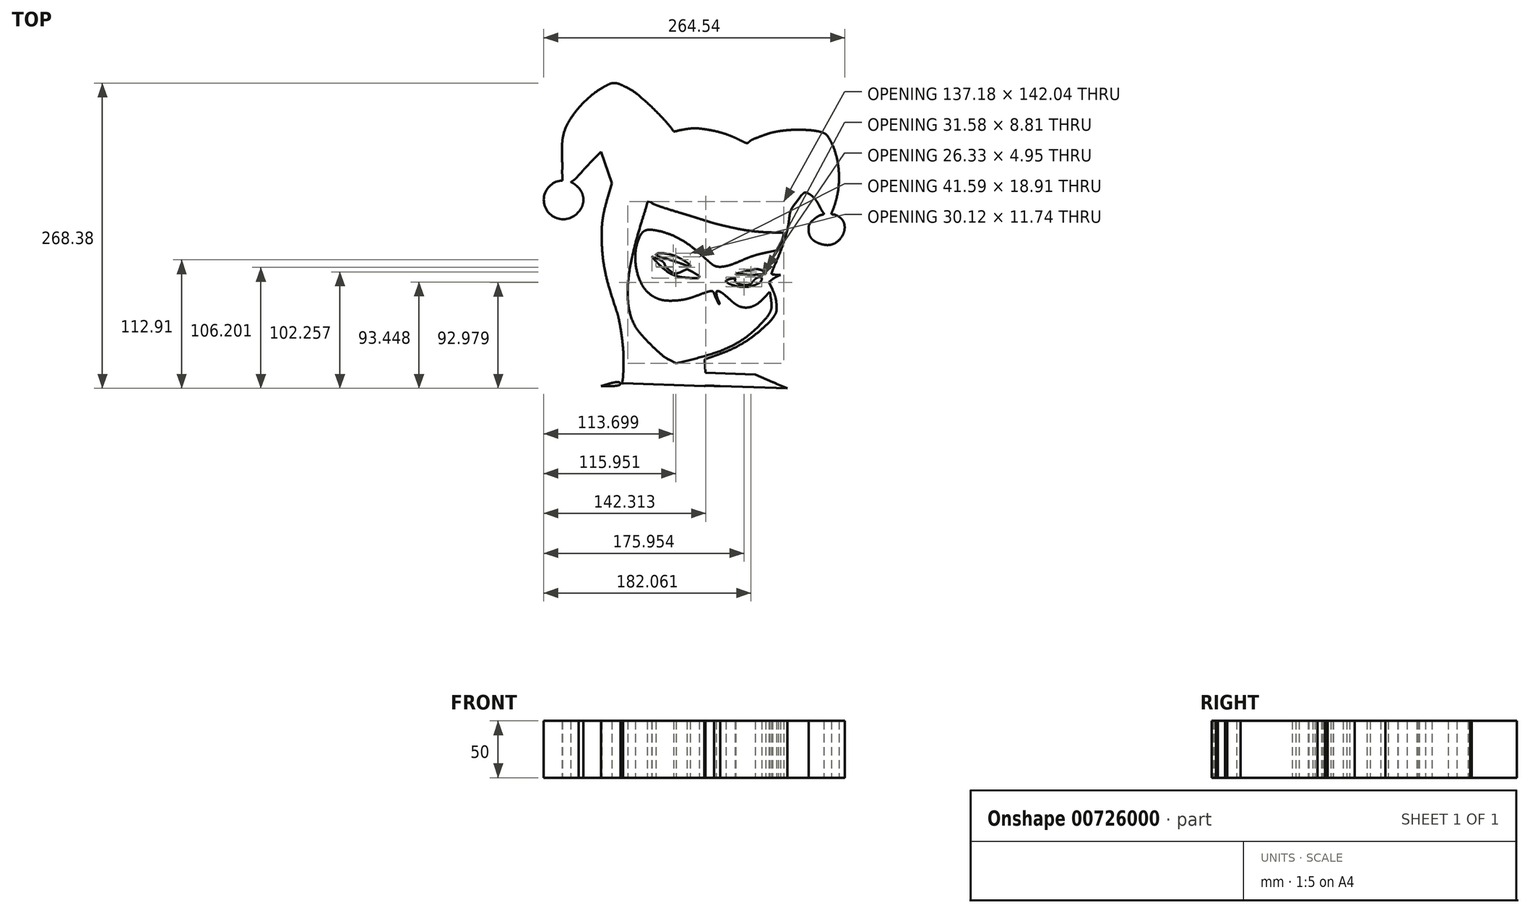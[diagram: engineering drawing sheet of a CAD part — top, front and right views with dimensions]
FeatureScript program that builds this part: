
annotation { "Feature Type Name" : "Feature", "Feature Type Description" : "" }
export const myFeature = defineFeature(function(context is Context, id is Id, definition is map)
    precondition{}
    {
        {
            var Q0;
            Q0=qCreatedBy(makeId("Top.planeOp"),FACE);
            var sketch = newSketch(context, id + "F0", { "sketchPlane" : qUnion([Q0])});
            skArc(sketch, "E0", {"start": v(-81.32, 129.17) * mm, "mid": v(-87.44, 125.11) * mm, "end": v(-93.17, 120.52) * mm});
            skArc(sketch, "E1", {"start": v(-93.17, 120.52) * mm, "mid": v(-98.64, 115.3) * mm, "end": v(-103.66, 109.63) * mm});
            skArc(sketch, "E2", {"start": v(-103.66, 109.63) * mm, "mid": v(-107.89, 103.97) * mm, "end": v(-111.61, 97.95) * mm});
            skArc(sketch, "E3", {"start": v(-111.61, 97.95) * mm, "mid": v(-114.1, 92.6) * mm, "end": v(-115.78, 86.95) * mm});
            skArc(sketch, "E4", {"start": v(-115.78, 86.95) * mm, "mid": v(-116.39, 83.45) * mm, "end": v(-116.67, 79.91) * mm});
            skArc(sketch, "E5", {"start": v(-116.67, 79.91) * mm, "mid": v(-116.8, 74.58) * mm, "end": v(-116.78, 69.25) * mm});
            skArc(sketch, "E6", {"start": v(-116.78, 69.25) * mm, "mid": v(-116.63, 64) * mm, "end": v(-116.35, 58.76) * mm});
            skArc(sketch, "E7", {"start": v(-116.35, 58.76) * mm, "mid": v(-116.71, 55.94) * mm, "end": v(-116.58, 53.1) * mm});
            skArc(sketch, "E8", {"start": v(-113.81, 56.72) * mm, "mid": v(-113.72, 62.46) * mm, "end": v(-113.64, 68.2) * mm});
            skArc(sketch, "E9", {"start": v(-113.64, 68.2) * mm, "mid": v(-113.48, 73.22) * mm, "end": v(-113.14, 78.23) * mm});
            skArc(sketch, "E10", {"start": v(-113.14, 78.23) * mm, "mid": v(-112.64, 82.07) * mm, "end": v(-111.84, 85.86) * mm});
            skArc(sketch, "E11", {"start": v(-111.84, 85.86) * mm, "mid": v(-110.77, 89.4) * mm, "end": v(-109.4, 92.83) * mm});
            skArc(sketch, "E12", {"start": v(-109.4, 92.83) * mm, "mid": v(-107.48, 96.82) * mm, "end": v(-105.36, 100.7) * mm});
            skArc(sketch, "E13", {"start": v(-105.36, 100.7) * mm, "mid": v(-102.38, 105.27) * mm, "end": v(-98.93, 109.5) * mm});
            skArc(sketch, "E14", {"start": v(-98.93, 109.5) * mm, "mid": v(-93.73, 114.95) * mm, "end": v(-88.31, 120.18) * mm});
            skArc(sketch, "E15", {"start": v(-88.31, 120.18) * mm, "mid": v(-82.87, 125.07) * mm, "end": v(-77.28, 129.78) * mm});
            skArc(sketch, "E16", {"start": v(-77.28, 129.78) * mm, "mid": v(-74.74, 131.2) * mm, "end": v(-71.87, 131.7) * mm});
            skArc(sketch, "E17", {"start": v(-71.87, 131.7) * mm, "mid": v(-70.1, 131.5) * mm, "end": v(-68.4, 130.9) * mm});
            skArc(sketch, "E18", {"start": v(-68.4, 130.9) * mm, "mid": v(-64.88, 129.08) * mm, "end": v(-61.4, 127.18) * mm});
            skArc(sketch, "E19", {"start": v(-61.4, 127.18) * mm, "mid": v(-57.7, 125) * mm, "end": v(-54.1, 122.7) * mm});
            skArc(sketch, "E20", {"start": v(-54.1, 122.7) * mm, "mid": v(-51.08, 120.58) * mm, "end": v(-48.19, 118.3) * mm});
            skArc(sketch, "E21", {"start": v(-48.19, 118.3) * mm, "mid": v(-43.26, 113.98) * mm, "end": v(-38.55, 109.45) * mm});
            skArc(sketch, "E22", {"start": v(-38.55, 109.45) * mm, "mid": v(-33.2, 103.92) * mm, "end": v(-28.02, 98.23) * mm});
            skArc(sketch, "E23", {"start": v(-28.02, 98.23) * mm, "mid": v(-23.22, 92.72) * mm, "end": v(-18.5, 87.13) * mm});
            skArc(sketch, "E24", {"start": v(-18.5, 87.13) * mm, "mid": v(-17.44, 85.27) * mm, "end": v(-17.07, 83.16) * mm});
            skArc(sketch, "E25", {"start": v(-17.07, 83.16) * mm, "mid": v(-17.14, 82.51) * mm, "end": v(-17.33, 81.9) * mm});
            skArc(sketch, "E26", {"start": v(-17.33, 81.9) * mm, "mid": v(-17.96, 80.48) * mm, "end": v(-18.61, 79.08) * mm});
            skArc(sketch, "E27", {"start": v(-18.61, 79.08) * mm, "mid": v(-19.44, 77.4) * mm, "end": v(-20.31, 75.75) * mm});
            skArc(sketch, "E28", {"start": v(-20.31, 75.75) * mm, "mid": v(-21.3, 73.96) * mm, "end": v(-22.32, 72.2) * mm});
            skArc(sketch, "E29", {"start": v(-22.32, 72.2) * mm, "mid": v(-25.2, 67.7) * mm, "end": v(-28.37, 63.39) * mm});
            skArc(sketch, "E30", {"start": v(-28.37, 63.39) * mm, "mid": v(-32.27, 58.69) * mm, "end": v(-36.38, 54.17) * mm});
            skArc(sketch, "E31", {"start": v(-36.38, 54.17) * mm, "mid": v(-40.75, 49.77) * mm, "end": v(-45.31, 45.58) * mm});
            skArc(sketch, "E32", {"start": v(-45.31, 45.58) * mm, "mid": v(-49.65, 42) * mm, "end": v(-54.2, 38.67) * mm});
            skArc(sketch, "E33", {"start": v(-54.2, 38.67) * mm, "mid": v(-56.08, 37.36) * mm, "end": v(-57.94, 36) * mm});
            skArc(sketch, "E34", {"start": v(-57.94, 36) * mm, "mid": v(-59.29, 34.97) * mm, "end": v(-60.59, 33.88) * mm});
            skArc(sketch, "E35", {"start": v(-60.59, 33.88) * mm, "mid": v(-61.47, 33.07) * mm, "end": v(-62.31, 32.22) * mm});
            skArc(sketch, "E36", {"start": v(-62.31, 32.22) * mm, "mid": v(-62.44, 31.96) * mm, "end": v(-62.4, 31.67) * mm});
            skArc(sketch, "E37", {"start": v(-60.44, 31.27) * mm, "mid": v(-57.35, 33) * mm, "end": v(-54.3, 34.83) * mm});
            skArc(sketch, "E38", {"start": v(-54.3, 34.83) * mm, "mid": v(-50.86, 37.06) * mm, "end": v(-47.5, 39.45) * mm});
            skArc(sketch, "E39", {"start": v(-47.5, 39.45) * mm, "mid": v(-44.24, 42) * mm, "end": v(-41.07, 44.67) * mm});
            skArc(sketch, "E40", {"start": v(-41.07, 44.67) * mm, "mid": v(-40.56, 45.12) * mm, "end": v(-40.04, 45.57) * mm});
            skArc(sketch, "E41", {"start": v(-40.04, 45.57) * mm, "mid": v(-39.53, 46) * mm, "end": v(-39, 46.43) * mm});
            skArc(sketch, "E42", {"start": v(-39, 46.43) * mm, "mid": v(-38.56, 46.79) * mm, "end": v(-38.1, 47.15) * mm});
            skArc(sketch, "E43", {"start": v(-38.1, 47.15) * mm, "mid": v(-37.83, 47.35) * mm, "end": v(-37.56, 47.54) * mm});
            skArc(sketch, "E44", {"start": v(-37.56, 47.54) * mm, "mid": v(-37.22, 47.8) * mm, "end": v(-36.9, 48.08) * mm});
            skArc(sketch, "E45", {"start": v(-36.9, 48.08) * mm, "mid": v(-35.83, 49.22) * mm, "end": v(-34.75, 50.36) * mm});
            skArc(sketch, "E46", {"start": v(-34.75, 50.36) * mm, "mid": v(-33.48, 51.72) * mm, "end": v(-32.23, 53.1) * mm});
            skArc(sketch, "E47", {"start": v(-32.23, 53.1) * mm, "mid": v(-30.82, 54.64) * mm, "end": v(-29.43, 56.2) * mm});
            skArc(sketch, "E48", {"start": v(-29.43, 56.2) * mm, "mid": v(-25.77, 60.56) * mm, "end": v(-22.36, 65.1) * mm});
            skArc(sketch, "E49", {"start": v(-22.36, 65.1) * mm, "mid": v(-19.43, 69.57) * mm, "end": v(-16.8, 74.22) * mm});
            skArc(sketch, "E50", {"start": v(-16.8, 74.22) * mm, "mid": v(-14.97, 78.05) * mm, "end": v(-13.4, 81.99) * mm});
            skArc(sketch, "E51", {"start": v(-13.4, 81.99) * mm, "mid": v(-13.34, 83.75) * mm, "end": v(-14.35, 85.19) * mm});
            skArc(sketch, "E52", {"start": v(-14.35, 85.19) * mm, "mid": v(-14.7, 85.49) * mm, "end": v(-15.03, 85.82) * mm});
            skArc(sketch, "E53", {"start": v(-15.03, 85.82) * mm, "mid": v(-15.55, 86.42) * mm, "end": v(-16.06, 87.04) * mm});
            skArc(sketch, "E54", {"start": v(-16.06, 87.04) * mm, "mid": v(-16.64, 87.77) * mm, "end": v(-17.2, 88.51) * mm});
            skArc(sketch, "E55", {"start": v(-17.2, 88.51) * mm, "mid": v(-17.76, 89.28) * mm, "end": v(-18.3, 90.07) * mm});
            skArc(sketch, "E56", {"start": v(-18.3, 90.07) * mm, "mid": v(-22.18, 95.38) * mm, "end": v(-26.43, 100.4) * mm});
            skArc(sketch, "E57", {"start": v(-26.43, 100.4) * mm, "mid": v(-32.2, 106.5) * mm, "end": v(-38.19, 112.41) * mm});
            skArc(sketch, "E58", {"start": v(-38.19, 112.41) * mm, "mid": v(-44.17, 117.91) * mm, "end": v(-50.34, 123.21) * mm});
            skArc(sketch, "E59", {"start": v(-50.34, 123.21) * mm, "mid": v(-54.65, 126.4) * mm, "end": v(-59.3, 129.09) * mm});
            skArc(sketch, "E60", {"start": v(-59.3, 129.09) * mm, "mid": v(-62.9, 130.82) * mm, "end": v(-66.58, 132.41) * mm});
            skArc(sketch, "E61", {"start": v(-66.58, 132.41) * mm, "mid": v(-68.75, 133.07) * mm, "end": v(-71, 133.3) * mm});
            skArc(sketch, "E62", {"start": v(-71, 133.3) * mm, "mid": v(-73.15, 133.07) * mm, "end": v(-75.2, 132.4) * mm});
            skArc(sketch, "E63", {"start": v(-75.2, 132.4) * mm, "mid": v(-78.3, 130.87) * mm, "end": v(-81.32, 129.17) * mm});
            skArc(sketch, "E64", {"start": v(-9.05, 92.56) * mm, "mid": v(-13.84, 91.64) * mm, "end": v(-18.58, 90.47) * mm});
            skLineSegment(sketch, "E65", {"start": v(11.05, 89.96) * mm, "end": v(14.74, 87) * mm});
            skArc(sketch, "E66", {"start": v(14.74, 87) * mm, "mid": v(15.68, 86.18) * mm, "end": v(16.55, 85.29) * mm});
            skArc(sketch, "E67", {"start": v(16.55, 85.29) * mm, "mid": v(17.85, 83.8) * mm, "end": v(19.1, 82.3) * mm});
            skArc(sketch, "E68", {"start": v(19.1, 82.3) * mm, "mid": v(20.5, 80.55) * mm, "end": v(21.86, 78.77) * mm});
            skArc(sketch, "E69", {"start": v(21.86, 78.77) * mm, "mid": v(23.17, 76.97) * mm, "end": v(24.43, 75.14) * mm});
            skLineSegment(sketch, "E70", {"start": v(30.43, 66.23) * mm, "end": v(30.26, 48.22) * mm});
            skArc(sketch, "E71", {"start": v(30.26, 48.22) * mm, "mid": v(30.19, 43.8) * mm, "end": v(30.07, 39.4) * mm});
            skArc(sketch, "E72", {"start": v(30.07, 39.4) * mm, "mid": v(29.91, 35.74) * mm, "end": v(29.68, 32.09) * mm});
            skArc(sketch, "E73", {"start": v(29.68, 32.09) * mm, "mid": v(29.42, 28.95) * mm, "end": v(29.08, 25.82) * mm});
            skArc(sketch, "E74", {"start": v(29.08, 25.82) * mm, "mid": v(28.69, 23) * mm, "end": v(28.21, 20.2) * mm});
            skArc(sketch, "E75", {"start": v(28.21, 20.2) * mm, "mid": v(27.6, 17.05) * mm, "end": v(26.98, 13.9) * mm});
            skArc(sketch, "E76", {"start": v(26.98, 13.9) * mm, "mid": v(26.68, 12.75) * mm, "end": v(26.26, 11.64) * mm});
            skArc(sketch, "E77", {"start": v(26.26, 11.64) * mm, "mid": v(25.88, 11.1) * mm, "end": v(25.33, 10.7) * mm});
            skArc(sketch, "E78", {"start": v(25.33, 10.7) * mm, "mid": v(24.63, 10.49) * mm, "end": v(23.88, 10.46) * mm});
            skArc(sketch, "E79", {"start": v(23.88, 10.46) * mm, "mid": v(22.5, 10.67) * mm, "end": v(21.13, 11) * mm});
            skArc(sketch, "E80", {"start": v(21.13, 11) * mm, "mid": v(16.22, 12.45) * mm, "end": v(11.31, 13.91) * mm});
            skArc(sketch, "E81", {"start": v(11.31, 13.91) * mm, "mid": v(4.2, 16.06) * mm, "end": v(-2.9, 18.24) * mm});
            skArc(sketch, "E82", {"start": v(-25.89, 25.38) * mm, "mid": v(-28.07, 26.05) * mm, "end": v(-30.26, 26.7) * mm});
            skArc(sketch, "E83", {"start": v(-30.26, 26.7) * mm, "mid": v(-32.14, 27.22) * mm, "end": v(-34.03, 27.72) * mm});
            skArc(sketch, "E84", {"start": v(-37.72, 28.39) * mm, "mid": v(-37.88, 27.88) * mm, "end": v(-37.55, 27.45) * mm});
            skArc(sketch, "E85", {"start": v(-37.55, 27.45) * mm, "mid": v(-35.57, 26.58) * mm, "end": v(-33.56, 25.79) * mm});
            skArc(sketch, "E86", {"start": v(-33.56, 25.79) * mm, "mid": v(-30.1, 24.54) * mm, "end": v(-26.6, 23.38) * mm});
            skArc(sketch, "E87", {"start": v(-26.6, 23.38) * mm, "mid": v(-19.94, 21.3) * mm, "end": v(-13.27, 19.23) * mm});
            skArc(sketch, "E88", {"start": v(-13.27, 19.23) * mm, "mid": v(-9.06, 17.93) * mm, "end": v(-4.85, 16.64) * mm});
            skArc(sketch, "E89", {"start": v(-4.85, 16.64) * mm, "mid": v(-0.76, 15.38) * mm, "end": v(3.34, 14.11) * mm});
            skArc(sketch, "E90", {"start": v(3.34, 14.11) * mm, "mid": v(6.84, 13.03) * mm, "end": v(10.35, 11.94) * mm});
            skArc(sketch, "E91", {"start": v(10.35, 11.94) * mm, "mid": v(12.27, 11.35) * mm, "end": v(14.2, 10.74) * mm});
            skArc(sketch, "E92", {"start": v(14.2, 10.74) * mm, "mid": v(15.97, 10.2) * mm, "end": v(17.77, 9.72) * mm});
            skArc(sketch, "E93", {"start": v(17.77, 9.72) * mm, "mid": v(20.53, 9.01) * mm, "end": v(23.3, 8.33) * mm});
            skArc(sketch, "E94", {"start": v(23.3, 8.33) * mm, "mid": v(26.43, 7.58) * mm, "end": v(29.56, 6.86) * mm});
            skArc(sketch, "E95", {"start": v(29.56, 6.86) * mm, "mid": v(32.62, 6.18) * mm, "end": v(35.7, 5.52) * mm});
            skArc(sketch, "E96", {"start": v(35.7, 5.52) * mm, "mid": v(40.58, 4.57) * mm, "end": v(45.48, 3.75) * mm});
            skArc(sketch, "E97", {"start": v(45.48, 3.75) * mm, "mid": v(50.3, 3.1) * mm, "end": v(55.12, 2.58) * mm});
            skArc(sketch, "E98", {"start": v(55.12, 2.58) * mm, "mid": v(60.3, 2.18) * mm, "end": v(65.47, 1.92) * mm});
            skArc(sketch, "E99", {"start": v(65.47, 1.92) * mm, "mid": v(71.47, 1.76) * mm, "end": v(77.47, 1.7) * mm});
            skArc(sketch, "E100", {"start": v(77.47, 1.7) * mm, "mid": v(77.8, 1.58) * mm, "end": v(78, 1.28) * mm});
            skArc(sketch, "E101", {"start": v(78, 1.28) * mm, "mid": v(78.07, 0.7) * mm, "end": v(78.03, 0.13) * mm});
            skArc(sketch, "E102", {"start": v(78.03, 0.13) * mm, "mid": v(77.8, -0.96) * mm, "end": v(77.48, -2.03) * mm});
            skArc(sketch, "E103", {"start": v(77.48, -2.03) * mm, "mid": v(76.81, -4) * mm, "end": v(76.12, -5.96) * mm});
            skLineSegment(sketch, "E104", {"start": v(76.12, -5.96) * mm, "end": v(73.34, -13.62) * mm});
            skLineSegment(sketch, "E105", {"start": v(73.34, -13.62) * mm, "end": v(64.38, -15.47) * mm});
            skArc(sketch, "E106", {"start": v(64.38, -15.47) * mm, "mid": v(60.62, -16.27) * mm, "end": v(56.88, -17.13) * mm});
            skArc(sketch, "E107", {"start": v(56.88, -17.13) * mm, "mid": v(54.29, -17.8) * mm, "end": v(51.73, -18.56) * mm});
            skArc(sketch, "E108", {"start": v(51.73, -18.56) * mm, "mid": v(49.08, -19.48) * mm, "end": v(46.46, -20.49) * mm});
            skArc(sketch, "E109", {"start": v(46.46, -20.49) * mm, "mid": v(42.37, -22.18) * mm, "end": v(38.29, -23.92) * mm});
            skArc(sketch, "E110", {"start": v(38.29, -23.92) * mm, "mid": v(34.67, -25.4) * mm, "end": v(31, -26.71) * mm});
            skArc(sketch, "E111", {"start": v(31, -26.71) * mm, "mid": v(28.1, -27.55) * mm, "end": v(25.14, -28.12) * mm});
            skArc(sketch, "E112", {"start": v(25.14, -28.12) * mm, "mid": v(22.78, -28.33) * mm, "end": v(20.4, -28.26) * mm});
            skArc(sketch, "E113", {"start": v(20.4, -28.26) * mm, "mid": v(18.45, -27.9) * mm, "end": v(16.61, -27.14) * mm});
            skArc(sketch, "E114", {"start": v(16.61, -27.14) * mm, "mid": v(15.96, -26.76) * mm, "end": v(15.35, -26.3) * mm});
            skArc(sketch, "E115", {"start": v(15.35, -26.3) * mm, "mid": v(14.04, -25.24) * mm, "end": v(12.75, -24.15) * mm});
            skArc(sketch, "E116", {"start": v(12.75, -24.15) * mm, "mid": v(11.22, -22.83) * mm, "end": v(9.7, -21.5) * mm});
            skArc(sketch, "E117", {"start": v(9.7, -21.5) * mm, "mid": v(8.1, -20.04) * mm, "end": v(6.52, -18.57) * mm});
            skArc(sketch, "E118", {"start": v(6.52, -18.57) * mm, "mid": v(1.86, -14.42) * mm, "end": v(-3.01, -10.51) * mm});
            skArc(sketch, "E119", {"start": v(-3.01, -10.51) * mm, "mid": v(-7.68, -7.2) * mm, "end": v(-12.56, -4.22) * mm});
            skArc(sketch, "E120", {"start": v(-12.56, -4.22) * mm, "mid": v(-17.29, -1.76) * mm, "end": v(-22.18, 0.35) * mm});
            skArc(sketch, "E121", {"start": v(-22.18, 0.35) * mm, "mid": v(-27.02, 2) * mm, "end": v(-31.97, 3.25) * mm});
            skArc(sketch, "E122", {"start": v(-31.97, 3.25) * mm, "mid": v(-35.4, 3.86) * mm, "end": v(-38.87, 4.28) * mm});
            skArc(sketch, "E123", {"start": v(-38.87, 4.28) * mm, "mid": v(-41.08, 4.25) * mm, "end": v(-43.25, 3.77) * mm});
            skArc(sketch, "E124", {"start": v(-43.25, 3.77) * mm, "mid": v(-44.94, 2.93) * mm, "end": v(-46.33, 1.66) * mm});
            skArc(sketch, "E125", {"start": v(-46.33, 1.66) * mm, "mid": v(-47.73, -0.28) * mm, "end": v(-48.84, -2.4) * mm});
            skArc(sketch, "E126", {"start": v(-48.84, -2.4) * mm, "mid": v(-51.16, -9.17) * mm, "end": v(-52.28, -16.24) * mm});
            skArc(sketch, "E127", {"start": v(-52.28, -16.24) * mm, "mid": v(-52.28, -23.84) * mm, "end": v(-51.2, -31.36) * mm});
            skArc(sketch, "E128", {"start": v(-51.2, -31.36) * mm, "mid": v(-49.11, -38.28) * mm, "end": v(-46.02, -44.8) * mm});
            skArc(sketch, "E129", {"start": v(-46.02, -44.8) * mm, "mid": v(-42.34, -49.78) * mm, "end": v(-37.58, -53.75) * mm});
            skArc(sketch, "E130", {"start": v(-37.58, -53.75) * mm, "mid": v(-35.43, -55.03) * mm, "end": v(-33.19, -56.11) * mm});
            skArc(sketch, "E131", {"start": v(-33.19, -56.11) * mm, "mid": v(-31, -56.93) * mm, "end": v(-28.75, -57.52) * mm});
            skArc(sketch, "E132", {"start": v(-28.75, -57.52) * mm, "mid": v(-26.2, -57.93) * mm, "end": v(-23.62, -58.12) * mm});
            skArc(sketch, "E133", {"start": v(-23.62, -58.12) * mm, "mid": v(-20.34, -58.14) * mm, "end": v(-17.07, -58.01) * mm});
            skArc(sketch, "E134", {"start": v(-17.07, -58.01) * mm, "mid": v(-14.77, -57.83) * mm, "end": v(-12.47, -57.57) * mm});
            skArc(sketch, "E135", {"start": v(-12.47, -57.57) * mm, "mid": v(-10.35, -57.23) * mm, "end": v(-8.24, -56.8) * mm});
            skArc(sketch, "E136", {"start": v(-8.24, -56.8) * mm, "mid": v(-6.02, -56.26) * mm, "end": v(-3.82, -55.62) * mm});
            skArc(sketch, "E137", {"start": v(-3.82, -55.62) * mm, "mid": v(-1.18, -54.75) * mm, "end": v(1.43, -53.83) * mm});
            skArc(sketch, "E138", {"start": v(1.43, -53.83) * mm, "mid": v(5.95, -52.2) * mm, "end": v(10.48, -50.57) * mm});
            skArc(sketch, "E139", {"start": v(10.48, -50.57) * mm, "mid": v(12.13, -50.06) * mm, "end": v(13.83, -49.67) * mm});
            skArc(sketch, "E140", {"start": v(13.83, -49.67) * mm, "mid": v(14.7, -49.63) * mm, "end": v(15.53, -49.84) * mm});
            skArc(sketch, "E141", {"start": v(15.53, -49.84) * mm, "mid": v(16.16, -50.28) * mm, "end": v(16.55, -50.93) * mm});
            skArc(sketch, "E142", {"start": v(16.55, -50.93) * mm, "mid": v(17.23, -52.8) * mm, "end": v(17.97, -54.66) * mm});
            skArc(sketch, "E143", {"start": v(17.97, -54.66) * mm, "mid": v(18.71, -56.4) * mm, "end": v(19.52, -58.11) * mm});
            skArc(sketch, "E144", {"start": v(19.52, -58.11) * mm, "mid": v(20.24, -59.55) * mm, "end": v(20.99, -60.97) * mm});
            skArc(sketch, "E145", {"start": v(20.99, -60.97) * mm, "mid": v(21.23, -61.14) * mm, "end": v(21.51, -61.04) * mm});
            skArc(sketch, "E146", {"start": v(21.51, -61.04) * mm, "mid": v(21.63, -60.86) * mm, "end": v(21.64, -60.65) * mm});
            skArc(sketch, "E147", {"start": v(21.64, -60.65) * mm, "mid": v(21.56, -60.2) * mm, "end": v(21.45, -59.75) * mm});
            skArc(sketch, "E148", {"start": v(21.45, -59.75) * mm, "mid": v(21.27, -59.2) * mm, "end": v(21.06, -58.65) * mm});
            skArc(sketch, "E149", {"start": v(21.06, -58.65) * mm, "mid": v(20.8, -58.04) * mm, "end": v(20.5, -57.44) * mm});
            skArc(sketch, "E150", {"start": v(20.5, -57.44) * mm, "mid": v(20.18, -56.77) * mm, "end": v(19.9, -56.08) * mm});
            skArc(sketch, "E151", {"start": v(19.9, -56.08) * mm, "mid": v(19.63, -55.3) * mm, "end": v(19.4, -54.52) * mm});
            skArc(sketch, "E152", {"start": v(19.4, -54.52) * mm, "mid": v(19.2, -53.76) * mm, "end": v(19.04, -53) * mm});
            skArc(sketch, "E153", {"start": v(19.04, -53) * mm, "mid": v(18.96, -52.4) * mm, "end": v(18.93, -51.78) * mm});
            skArc(sketch, "E154", {"start": v(18.93, -51.78) * mm, "mid": v(18.95, -51.07) * mm, "end": v(19, -50.36) * mm});
            skArc(sketch, "E155", {"start": v(19, -50.36) * mm, "mid": v(19.11, -50.02) * mm, "end": v(19.33, -49.75) * mm});
            skArc(sketch, "E156", {"start": v(19.33, -49.75) * mm, "mid": v(19.62, -49.59) * mm, "end": v(19.95, -49.57) * mm});
            skArc(sketch, "E157", {"start": v(19.95, -49.57) * mm, "mid": v(20.57, -49.68) * mm, "end": v(21.18, -49.84) * mm});
            skArc(sketch, "E158", {"start": v(21.18, -49.84) * mm, "mid": v(21.73, -50.03) * mm, "end": v(22.25, -50.29) * mm});
            skArc(sketch, "E159", {"start": v(22.25, -50.29) * mm, "mid": v(22.96, -50.69) * mm, "end": v(23.65, -51.12) * mm});
            skArc(sketch, "E160", {"start": v(23.65, -51.12) * mm, "mid": v(24.4, -51.62) * mm, "end": v(25.12, -52.15) * mm});
            skArc(sketch, "E161", {"start": v(25.12, -52.15) * mm, "mid": v(25.78, -52.68) * mm, "end": v(26.43, -53.24) * mm});
            skArc(sketch, "E162", {"start": v(26.43, -53.24) * mm, "mid": v(28.9, -55.47) * mm, "end": v(31.37, -57.68) * mm});
            skArc(sketch, "E163", {"start": v(31.37, -57.68) * mm, "mid": v(32.77, -58.9) * mm, "end": v(34.22, -60.06) * mm});
            skArc(sketch, "E164", {"start": v(34.22, -60.06) * mm, "mid": v(35.27, -60.85) * mm, "end": v(36.37, -61.59) * mm});
            skArc(sketch, "E165", {"start": v(36.37, -61.59) * mm, "mid": v(37.45, -62.22) * mm, "end": v(38.57, -62.8) * mm});
            skArc(sketch, "E166", {"start": v(38.57, -62.8) * mm, "mid": v(41.25, -63.76) * mm, "end": v(44.06, -64.18) * mm});
            skArc(sketch, "E167", {"start": v(44.06, -64.18) * mm, "mid": v(46.96, -64.07) * mm, "end": v(49.8, -63.43) * mm});
            skArc(sketch, "E168", {"start": v(49.8, -63.43) * mm, "mid": v(52.79, -62.18) * mm, "end": v(55.55, -60.47) * mm});
            skArc(sketch, "E169", {"start": v(55.55, -60.47) * mm, "mid": v(58.46, -58.1) * mm, "end": v(61.12, -55.43) * mm});
            skLineSegment(sketch, "E170", {"start": v(61.12, -55.43) * mm, "end": v(65.76, -50.26) * mm});
            skLineSegment(sketch, "E171", {"start": v(65.76, -50.26) * mm, "end": v(66.3, -53.03) * mm});
            skArc(sketch, "E172", {"start": v(66.3, -53.03) * mm, "mid": v(66.97, -57.23) * mm, "end": v(67.4, -61.47) * mm});
            skArc(sketch, "E173", {"start": v(67.4, -61.47) * mm, "mid": v(67.33, -64.2) * mm, "end": v(66.7, -66.85) * mm});
            skArc(sketch, "E174", {"start": v(66.7, -66.85) * mm, "mid": v(65.49, -69.51) * mm, "end": v(63.83, -71.92) * mm});
            skArc(sketch, "E175", {"start": v(63.83, -71.92) * mm, "mid": v(60.46, -75.86) * mm, "end": v(56.95, -79.67) * mm});
            skArc(sketch, "E176", {"start": v(56.95, -79.67) * mm, "mid": v(51.35, -85.06) * mm, "end": v(45.32, -89.96) * mm});
            skArc(sketch, "E177", {"start": v(45.32, -89.96) * mm, "mid": v(39, -94.24) * mm, "end": v(32.33, -97.94) * mm});
            skArc(sketch, "E178", {"start": v(32.33, -97.94) * mm, "mid": v(24.46, -101.5) * mm, "end": v(16.35, -104.44) * mm});
            skArc(sketch, "E179", {"start": v(16.35, -104.44) * mm, "mid": v(5.97, -107.56) * mm, "end": v(-4.52, -110.27) * mm});
            skLineSegment(sketch, "E180", {"start": v(-4.52, -110.27) * mm, "end": v(-16.48, -113.12) * mm});
            skLineSegment(sketch, "E181", {"start": v(-16.48, -113.12) * mm, "end": v(-22.52, -110.1) * mm});
            skArc(sketch, "E182", {"start": v(-22.52, -110.1) * mm, "mid": v(-26.18, -107.99) * mm, "end": v(-29.53, -105.41) * mm});
            skArc(sketch, "E183", {"start": v(-29.53, -105.41) * mm, "mid": v(-34.53, -100.88) * mm, "end": v(-39.37, -96.19) * mm});
            skArc(sketch, "E184", {"start": v(-39.37, -96.19) * mm, "mid": v(-44.05, -91.32) * mm, "end": v(-48.56, -86.3) * mm});
            skArc(sketch, "E185", {"start": v(-48.56, -86.3) * mm, "mid": v(-51.14, -82.91) * mm, "end": v(-53.27, -79.23) * mm});
            skArc(sketch, "E186", {"start": v(-53.27, -79.23) * mm, "mid": v(-56.39, -71.43) * mm, "end": v(-58.22, -63.24) * mm});
            skArc(sketch, "E187", {"start": v(-58.22, -63.24) * mm, "mid": v(-59.06, -53.57) * mm, "end": v(-58.88, -43.86) * mm});
            skArc(sketch, "E188", {"start": v(-58.88, -43.86) * mm, "mid": v(-57.54, -31.75) * mm, "end": v(-55.25, -19.78) * mm});
            skArc(sketch, "E189", {"start": v(-55.25, -19.78) * mm, "mid": v(-51.37, -4.39) * mm, "end": v(-46.93, 10.85) * mm});
            skArc(sketch, "E190", {"start": v(-46.93, 10.85) * mm, "mid": v(-45.05, 16.91) * mm, "end": v(-43.18, 22.97) * mm});
            skArc(sketch, "E191", {"start": v(-43.18, 22.97) * mm, "mid": v(-42.6, 25) * mm, "end": v(-42.1, 27.05) * mm});
            skArc(sketch, "E192", {"start": v(-42.1, 27.05) * mm, "mid": v(-41.94, 28.04) * mm, "end": v(-41.91, 29.04) * mm});
            skArc(sketch, "E193", {"start": v(-44.45, 29.24) * mm, "mid": v(-44.58, 29.02) * mm, "end": v(-44.68, 28.77) * mm});
            skArc(sketch, "E194", {"start": v(-44.68, 28.77) * mm, "mid": v(-48.4, 16.2) * mm, "end": v(-52.09, 3.6) * mm});
            skArc(sketch, "E195", {"start": v(-52.09, 3.6) * mm, "mid": v(-55.44, -8.35) * mm, "end": v(-58.6, -20.35) * mm});
            skArc(sketch, "E196", {"start": v(-58.6, -20.35) * mm, "mid": v(-60.56, -28.92) * mm, "end": v(-62.13, -37.57) * mm});
            skArc(sketch, "E197", {"start": v(-62.13, -37.57) * mm, "mid": v(-62.63, -41.61) * mm, "end": v(-62.87, -45.68) * mm});
            skArc(sketch, "E198", {"start": v(-62.87, -45.68) * mm, "mid": v(-62.9, -50.7) * mm, "end": v(-62.77, -55.7) * mm});
            skArc(sketch, "E199", {"start": v(-62.77, -55.7) * mm, "mid": v(-62.47, -60.56) * mm, "end": v(-62, -65.4) * mm});
            skArc(sketch, "E200", {"start": v(-62, -65.4) * mm, "mid": v(-61.43, -68.88) * mm, "end": v(-60.56, -72.3) * mm});
            skArc(sketch, "E201", {"start": v(-60.56, -72.3) * mm, "mid": v(-59.08, -76.7) * mm, "end": v(-57.36, -81.02) * mm});
            skArc(sketch, "E202", {"start": v(-57.36, -81.02) * mm, "mid": v(-55.28, -85.56) * mm, "end": v(-53, -89.99) * mm});
            skArc(sketch, "E203", {"start": v(-53, -89.99) * mm, "mid": v(-50.66, -94.05) * mm, "end": v(-48.13, -98) * mm});
            skArc(sketch, "E204", {"start": v(-48.13, -98) * mm, "mid": v(-45.91, -100.97) * mm, "end": v(-43.43, -103.73) * mm});
            skArc(sketch, "E205", {"start": v(-43.43, -103.73) * mm, "mid": v(-41.13, -105.89) * mm, "end": v(-38.7, -107.89) * mm});
            skArc(sketch, "E206", {"start": v(-38.7, -107.89) * mm, "mid": v(-36.14, -109.7) * mm, "end": v(-33.47, -111.35) * mm});
            skArc(sketch, "E207", {"start": v(-33.47, -111.35) * mm, "mid": v(-30.85, -112.7) * mm, "end": v(-28.13, -113.88) * mm});
            skArc(sketch, "E208", {"start": v(-28.13, -113.88) * mm, "mid": v(-25.64, -114.7) * mm, "end": v(-23.07, -115.26) * mm});
            skArc(sketch, "E209", {"start": v(-23.07, -115.26) * mm, "mid": v(-22.05, -115.45) * mm, "end": v(-21.04, -115.7) * mm});
            skArc(sketch, "E210", {"start": v(-21.04, -115.7) * mm, "mid": v(-20.53, -115.92) * mm, "end": v(-20.11, -116.28) * mm});
            skArc(sketch, "E211", {"start": v(-20.11, -116.28) * mm, "mid": v(-19.82, -116.74) * mm, "end": v(-19.68, -117.27) * mm});
            skArc(sketch, "E212", {"start": v(-19.68, -117.27) * mm, "mid": v(-19.6, -118.3) * mm, "end": v(-19.57, -119.31) * mm});
            skLineSegment(sketch, "E213", {"start": v(-19.57, -119.31) * mm, "end": v(-19.57, -122.8) * mm});
            skLineSegment(sketch, "E214", {"start": v(-19.57, -122.8) * mm, "end": v(-26.97, -123.1) * mm});
            skArc(sketch, "E215", {"start": v(-26.97, -123.1) * mm, "mid": v(-29.01, -123.13) * mm, "end": v(-31.05, -123.09) * mm});
            skArc(sketch, "E216", {"start": v(-31.05, -123.09) * mm, "mid": v(-33.01, -122.96) * mm, "end": v(-34.97, -122.74) * mm});
            skArc(sketch, "E217", {"start": v(-34.97, -122.74) * mm, "mid": v(-37.12, -122.4) * mm, "end": v(-39.25, -122) * mm});
            skArc(sketch, "E218", {"start": v(-39.25, -122) * mm, "mid": v(-41.87, -121.4) * mm, "end": v(-44.47, -120.74) * mm});
            skArc(sketch, "E219", {"start": v(-44.47, -120.74) * mm, "mid": v(-48.6, -119.66) * mm, "end": v(-52.7, -118.6) * mm});
            skArc(sketch, "E220", {"start": v(-52.7, -118.6) * mm, "mid": v(-53.92, -118.32) * mm, "end": v(-55.14, -118.1) * mm});
            skArc(sketch, "E221", {"start": v(-55.14, -118.1) * mm, "mid": v(-55.75, -118.07) * mm, "end": v(-56.34, -118.18) * mm});
            skArc(sketch, "E222", {"start": v(-56.34, -118.18) * mm, "mid": v(-56.77, -118.41) * mm, "end": v(-57.07, -118.8) * mm});
            skArc(sketch, "E223", {"start": v(-57.07, -118.8) * mm, "mid": v(-57.1, -119.09) * mm, "end": v(-56.91, -119.31) * mm});
            skArc(sketch, "E224", {"start": v(-56.91, -119.31) * mm, "mid": v(-55.93, -119.86) * mm, "end": v(-54.93, -120.37) * mm});
            skArc(sketch, "E225", {"start": v(-54.93, -120.37) * mm, "mid": v(-53.62, -120.98) * mm, "end": v(-52.3, -121.55) * mm});
            skArc(sketch, "E226", {"start": v(-52.3, -121.55) * mm, "mid": v(-50.69, -122.17) * mm, "end": v(-49.07, -122.75) * mm});
            skArc(sketch, "E227", {"start": v(-49.07, -122.75) * mm, "mid": v(-46.3, -123.66) * mm, "end": v(-43.51, -124.48) * mm});
            skArc(sketch, "E228", {"start": v(-43.51, -124.48) * mm, "mid": v(-41.4, -124.97) * mm, "end": v(-39.25, -125.3) * mm});
            skArc(sketch, "E229", {"start": v(-39.25, -125.3) * mm, "mid": v(-36.57, -125.53) * mm, "end": v(-33.87, -125.63) * mm});
            skArc(sketch, "E230", {"start": v(-33.87, -125.63) * mm, "mid": v(-28.22, -125.7) * mm, "end": v(-22.57, -125.71) * mm});
            skArc(sketch, "E231", {"start": v(-22.57, -125.71) * mm, "mid": v(-18.5, -125.7) * mm, "end": v(-14.44, -125.64) * mm});
            skArc(sketch, "E232", {"start": v(-14.44, -125.64) * mm, "mid": v(-11.21, -125.55) * mm, "end": v(-8, -125.4) * mm});
            skArc(sketch, "E233", {"start": v(-8, -125.4) * mm, "mid": v(-5.53, -125.22) * mm, "end": v(-3.07, -125) * mm});
            skArc(sketch, "E234", {"start": v(-3.07, -125) * mm, "mid": v(-1.58, -124.77) * mm, "end": v(-0.12, -124.42) * mm});
            skArc(sketch, "E235", {"start": v(-0.12, -124.42) * mm, "mid": v(1.18, -124.05) * mm, "end": v(2.5, -123.72) * mm});
            skArc(sketch, "E236", {"start": v(2.5, -123.72) * mm, "mid": v(3.15, -123.61) * mm, "end": v(3.81, -123.61) * mm});
            skArc(sketch, "E237", {"start": v(3.81, -123.61) * mm, "mid": v(4.3, -123.72) * mm, "end": v(4.73, -123.97) * mm});
            skArc(sketch, "E238", {"start": v(4.73, -123.97) * mm, "mid": v(5.21, -124.4) * mm, "end": v(5.63, -124.9) * mm});
            skArc(sketch, "E239", {"start": v(5.63, -124.9) * mm, "mid": v(5.9, -125.34) * mm, "end": v(6.13, -125.81) * mm});
            skArc(sketch, "E240", {"start": v(6.13, -125.81) * mm, "mid": v(6.36, -126.46) * mm, "end": v(6.55, -127.13) * mm});
            skArc(sketch, "E241", {"start": v(6.55, -127.13) * mm, "mid": v(6.71, -127.85) * mm, "end": v(6.83, -128.59) * mm});
            skArc(sketch, "E242", {"start": v(6.83, -128.59) * mm, "mid": v(6.9, -129.29) * mm, "end": v(6.93, -129.99) * mm});
            skArc(sketch, "E243", {"start": v(6.93, -129.99) * mm, "mid": v(6.95, -130.72) * mm, "end": v(7.01, -131.46) * mm});
            skArc(sketch, "E244", {"start": v(7.01, -131.46) * mm, "mid": v(7.11, -131.98) * mm, "end": v(7.29, -132.48) * mm});
            skArc(sketch, "E245", {"start": v(7.29, -132.48) * mm, "mid": v(7.48, -132.8) * mm, "end": v(7.75, -133.07) * mm});
            skArc(sketch, "E246", {"start": v(7.75, -133.07) * mm, "mid": v(8.04, -133.24) * mm, "end": v(8.38, -133.3) * mm});
            skArc(sketch, "E247", {"start": v(8.38, -133.3) * mm, "mid": v(8.83, -133.15) * mm, "end": v(9.11, -132.77) * mm});
            skArc(sketch, "E248", {"start": v(9.11, -132.77) * mm, "mid": v(9.34, -131.95) * mm, "end": v(9.45, -131.1) * mm});
            skArc(sketch, "E249", {"start": v(9.45, -131.1) * mm, "mid": v(9.52, -129.53) * mm, "end": v(9.51, -127.94) * mm});
            skArc(sketch, "E250", {"start": v(9.51, -127.94) * mm, "mid": v(9.39, -124.7) * mm, "end": v(9.23, -121.47) * mm});
            skLineSegment(sketch, "E251", {"start": v(9.24, -121.47) * mm, "end": v(8.64, -109.64) * mm});
            skLineSegment(sketch, "E252", {"start": v(8.64, -109.64) * mm, "end": v(19.53, -105.9) * mm});
            skArc(sketch, "E253", {"start": v(19.53, -105.9) * mm, "mid": v(23.63, -104.42) * mm, "end": v(27.68, -102.82) * mm});
            skArc(sketch, "E254", {"start": v(27.68, -102.82) * mm, "mid": v(31.4, -101.2) * mm, "end": v(35.07, -99.46) * mm});
            skArc(sketch, "E255", {"start": v(35.07, -99.46) * mm, "mid": v(38.52, -97.65) * mm, "end": v(41.91, -95.71) * mm});
            skArc(sketch, "E256", {"start": v(41.91, -95.71) * mm, "mid": v(45.21, -93.65) * mm, "end": v(48.43, -91.46) * mm});
            skArc(sketch, "E257", {"start": v(48.43, -91.46) * mm, "mid": v(51.6, -89.14) * mm, "end": v(54.68, -86.73) * mm});
            skArc(sketch, "E258", {"start": v(54.68, -86.73) * mm, "mid": v(57.74, -84.18) * mm, "end": v(60.71, -81.54) * mm});
            skArc(sketch, "E259", {"start": v(60.71, -81.54) * mm, "mid": v(63.3, -79.1) * mm, "end": v(65.83, -76.56) * mm});
            skArc(sketch, "E260", {"start": v(65.83, -76.56) * mm, "mid": v(67.53, -74.65) * mm, "end": v(69.06, -72.6) * mm});
            skArc(sketch, "E261", {"start": v(69.06, -72.6) * mm, "mid": v(69.96, -71.23) * mm, "end": v(70.8, -69.82) * mm});
            skArc(sketch, "E262", {"start": v(70.8, -69.82) * mm, "mid": v(71.28, -68.83) * mm, "end": v(71.6, -67.78) * mm});
            skArc(sketch, "E263", {"start": v(71.6, -67.78) * mm, "mid": v(71.81, -66.63) * mm, "end": v(71.88, -65.46) * mm});
            skArc(sketch, "E264", {"start": v(71.88, -65.46) * mm, "mid": v(71.84, -63.46) * mm, "end": v(71.74, -61.46) * mm});
            skArc(sketch, "E265", {"start": v(71.74, -61.46) * mm, "mid": v(71.6, -59.71) * mm, "end": v(71.38, -57.98) * mm});
            skArc(sketch, "E266", {"start": v(71.38, -57.98) * mm, "mid": v(71.1, -56.4) * mm, "end": v(70.72, -54.83) * mm});
            skArc(sketch, "E267", {"start": v(70.72, -54.83) * mm, "mid": v(70.24, -53.26) * mm, "end": v(69.68, -51.71) * mm});
            skArc(sketch, "E268", {"start": v(69.68, -51.71) * mm, "mid": v(68.96, -49.99) * mm, "end": v(68.18, -48.3) * mm});
            skLineSegment(sketch, "E269", {"start": v(68.18, -48.3) * mm, "end": v(65.01, -41.8) * mm});
            skLineSegment(sketch, "E270", {"start": v(65.01, -41.8) * mm, "end": v(67.22, -39.98) * mm});
            skArc(sketch, "E271", {"start": v(67.22, -39.98) * mm, "mid": v(67.74, -39.57) * mm, "end": v(68.28, -39.19) * mm});
            skArc(sketch, "E272", {"start": v(68.28, -39.19) * mm, "mid": v(68.97, -38.73) * mm, "end": v(69.66, -38.3) * mm});
            skArc(sketch, "E273", {"start": v(69.66, -38.3) * mm, "mid": v(70.39, -37.86) * mm, "end": v(71.12, -37.44) * mm});
            skArc(sketch, "E274", {"start": v(71.12, -37.44) * mm, "mid": v(71.77, -37.1) * mm, "end": v(72.43, -36.77) * mm});
            skLineSegment(sketch, "E275", {"start": v(72.43, -36.77) * mm, "end": v(75.43, -35.37) * mm});
            skLineSegment(sketch, "E276", {"start": v(75.43, -35.37) * mm, "end": v(71.74, -35.33) * mm});
            skArc(sketch, "E277", {"start": v(71.74, -35.33) * mm, "mid": v(71.01, -35.31) * mm, "end": v(70.29, -35.26) * mm});
            skArc(sketch, "E278", {"start": v(70.29, -35.26) * mm, "mid": v(69.64, -35.19) * mm, "end": v(68.99, -35.07) * mm});
            skArc(sketch, "E279", {"start": v(68.99, -35.07) * mm, "mid": v(68.47, -34.96) * mm, "end": v(67.96, -34.81) * mm});
            skArc(sketch, "E280", {"start": v(67.96, -34.81) * mm, "mid": v(67.73, -34.7) * mm, "end": v(67.56, -34.5) * mm});
            skArc(sketch, "E281", {"start": v(67.56, -34.5) * mm, "mid": v(67.46, -34.21) * mm, "end": v(67.49, -33.9) * mm});
            skArc(sketch, "E282", {"start": v(67.49, -33.9) * mm, "mid": v(67.93, -32.61) * mm, "end": v(68.4, -31.33) * mm});
            skArc(sketch, "E283", {"start": v(68.4, -31.33) * mm, "mid": v(68.97, -29.8) * mm, "end": v(69.59, -28.27) * mm});
            skArc(sketch, "E284", {"start": v(69.59, -28.27) * mm, "mid": v(70.33, -26.53) * mm, "end": v(71.1, -24.8) * mm});
            skArc(sketch, "E285", {"start": v(71.1, -24.8) * mm, "mid": v(73.32, -19.68) * mm, "end": v(75.38, -14.5) * mm});
            skArc(sketch, "E286", {"start": v(75.38, -14.5) * mm, "mid": v(77.23, -9.43) * mm, "end": v(78.92, -4.3) * mm});
            skArc(sketch, "E287", {"start": v(78.92, -4.3) * mm, "mid": v(80.28, 0.38) * mm, "end": v(81.48, 5.1) * mm});
            skArc(sketch, "E288", {"start": v(81.48, 5.1) * mm, "mid": v(82.26, 8.96) * mm, "end": v(82.78, 12.86) * mm});
            skArc(sketch, "E289", {"start": v(82.78, 12.86) * mm, "mid": v(83.1, 15.54) * mm, "end": v(83.47, 18.2) * mm});
            skArc(sketch, "E290", {"start": v(83.47, 18.2) * mm, "mid": v(83.81, 19.74) * mm, "end": v(84.33, 21.23) * mm});
            skArc(sketch, "E291", {"start": v(84.33, 21.23) * mm, "mid": v(85.07, 22.73) * mm, "end": v(85.96, 24.16) * mm});
            skArc(sketch, "E292", {"start": v(85.96, 24.16) * mm, "mid": v(87.85, 26.82) * mm, "end": v(89.8, 29.45) * mm});
            skArc(sketch, "E293", {"start": v(89.8, 29.45) * mm, "mid": v(91.76, 32.03) * mm, "end": v(93.74, 34.59) * mm});
            skArc(sketch, "E294", {"start": v(93.74, 34.59) * mm, "mid": v(94.56, 35.52) * mm, "end": v(95.48, 36.36) * mm});
            skArc(sketch, "E295", {"start": v(95.48, 36.36) * mm, "mid": v(96.15, 36.74) * mm, "end": v(96.91, 36.9) * mm});
            skArc(sketch, "E296", {"start": v(96.91, 36.9) * mm, "mid": v(97.82, 36.84) * mm, "end": v(98.7, 36.61) * mm});
            skArc(sketch, "E297", {"start": v(98.7, 36.61) * mm, "mid": v(100.21, 35.92) * mm, "end": v(101.63, 35.04) * mm});
            skArc(sketch, "E298", {"start": v(101.63, 35.04) * mm, "mid": v(103.11, 33.86) * mm, "end": v(104.49, 32.55) * mm});
            skArc(sketch, "E299", {"start": v(104.49, 32.55) * mm, "mid": v(105.85, 31.02) * mm, "end": v(107.08, 29.38) * mm});
            skArc(sketch, "E300", {"start": v(107.08, 29.38) * mm, "mid": v(108.2, 27.6) * mm, "end": v(109.18, 25.72) * mm});
            skArc(sketch, "E301", {"start": v(109.18, 25.72) * mm, "mid": v(109.64, 24.8) * mm, "end": v(110.1, 23.87) * mm});
            skArc(sketch, "E302", {"start": v(110.1, 23.87) * mm, "mid": v(110.6, 22.95) * mm, "end": v(111.1, 22.05) * mm});
            skArc(sketch, "E303", {"start": v(111.1, 22.05) * mm, "mid": v(111.57, 21.26) * mm, "end": v(112.04, 20.48) * mm});
            skArc(sketch, "E304", {"start": v(112.04, 20.48) * mm, "mid": v(112.36, 20) * mm, "end": v(112.7, 19.55) * mm});
            skArc(sketch, "E305", {"start": v(112.7, 19.55) * mm, "mid": v(113.05, 19.1) * mm, "end": v(113.35, 18.6) * mm});
            skArc(sketch, "E306", {"start": v(113.35, 18.6) * mm, "mid": v(113.41, 18.32) * mm, "end": v(113.31, 18.06) * mm});
            skArc(sketch, "E307", {"start": v(113.31, 18.06) * mm, "mid": v(113.05, 17.8) * mm, "end": v(112.72, 17.65) * mm});
            skArc(sketch, "E308", {"start": v(112.72, 17.65) * mm, "mid": v(111.84, 17.42) * mm, "end": v(110.94, 17.2) * mm});
            skArc(sketch, "E309", {"start": v(110.94, 17.2) * mm, "mid": v(110.2, 17) * mm, "end": v(109.47, 16.69) * mm});
            skArc(sketch, "E310", {"start": v(109.47, 16.69) * mm, "mid": v(108.51, 16.18) * mm, "end": v(107.58, 15.62) * mm});
            skArc(sketch, "E311", {"start": v(107.58, 15.62) * mm, "mid": v(106.58, 14.96) * mm, "end": v(105.61, 14.26) * mm});
            skArc(sketch, "E312", {"start": v(105.61, 14.26) * mm, "mid": v(104.73, 13.53) * mm, "end": v(103.87, 12.77) * mm});
            skArc(sketch, "E313", {"start": v(103.87, 12.77) * mm, "mid": v(102.79, 11.7) * mm, "end": v(101.74, 10.57) * mm});
            skArc(sketch, "E314", {"start": v(101.74, 10.57) * mm, "mid": v(101.13, 9.79) * mm, "end": v(100.63, 8.93) * mm});
            skArc(sketch, "E315", {"start": v(100.63, 8.93) * mm, "mid": v(100.3, 8.08) * mm, "end": v(100.1, 7.19) * mm});
            skArc(sketch, "E316", {"start": v(100.1, 7.19) * mm, "mid": v(99.97, 5.98) * mm, "end": v(99.93, 4.76) * mm});
            skArc(sketch, "E317", {"start": v(99.93, 4.76) * mm, "mid": v(100.05, 2.73) * mm, "end": v(100.42, 0.72) * mm});
            skArc(sketch, "E318", {"start": v(100.42, 0.72) * mm, "mid": v(101, -0.98) * mm, "end": v(101.88, -2.55) * mm});
            skArc(sketch, "E319", {"start": v(101.88, -2.55) * mm, "mid": v(103.02, -3.97) * mm, "end": v(104.4, -5.17) * mm});
            skArc(sketch, "E320", {"start": v(104.4, -5.17) * mm, "mid": v(106.17, -6.31) * mm, "end": v(108.06, -7.26) * mm});
            skArc(sketch, "E321", {"start": v(108.06, -7.26) * mm, "mid": v(111.05, -8.34) * mm, "end": v(114.16, -9.05) * mm});
            skArc(sketch, "E322", {"start": v(114.16, -9.05) * mm, "mid": v(116.87, -9.25) * mm, "end": v(119.58, -8.93) * mm});
            skArc(sketch, "E323", {"start": v(119.58, -8.93) * mm, "mid": v(122.06, -8.12) * mm, "end": v(124.33, -6.83) * mm});
            skArc(sketch, "E324", {"start": v(124.33, -6.83) * mm, "mid": v(126.55, -4.99) * mm, "end": v(128.47, -2.83) * mm});
            skArc(sketch, "E325", {"start": v(128.47, -2.83) * mm, "mid": v(129.6, -1.15) * mm, "end": v(130.5, 0.65) * mm});
            skArc(sketch, "E326", {"start": v(130.5, 0.65) * mm, "mid": v(131.17, 2.52) * mm, "end": v(131.57, 4.45) * mm});
            skArc(sketch, "E327", {"start": v(131.57, 4.45) * mm, "mid": v(131.7, 6.32) * mm, "end": v(131.58, 8.19) * mm});
            skArc(sketch, "E328", {"start": v(131.58, 8.19) * mm, "mid": v(131.2, 9.9) * mm, "end": v(130.52, 11.52) * mm});
            skArc(sketch, "E329", {"start": v(130.52, 11.52) * mm, "mid": v(129.8, 12.71) * mm, "end": v(128.9, 13.78) * mm});
            skArc(sketch, "E330", {"start": v(128.9, 13.78) * mm, "mid": v(127.74, 14.86) * mm, "end": v(126.48, 15.8) * mm});
            skArc(sketch, "E331", {"start": v(126.48, 15.8) * mm, "mid": v(125.17, 16.59) * mm, "end": v(123.8, 17.23) * mm});
            skArc(sketch, "E332", {"start": v(123.8, 17.23) * mm, "mid": v(122.6, 17.59) * mm, "end": v(121.37, 17.7) * mm});
            skArc(sketch, "E333", {"start": v(121.37, 17.7) * mm, "mid": v(121, 17.73) * mm, "end": v(120.64, 17.8) * mm});
            skArc(sketch, "E334", {"start": v(120.64, 17.8) * mm, "mid": v(120.42, 17.92) * mm, "end": v(120.27, 18.1) * mm});
            skArc(sketch, "E335", {"start": v(120.27, 18.1) * mm, "mid": v(120.18, 18.36) * mm, "end": v(120.2, 18.63) * mm});
            skArc(sketch, "E336", {"start": v(120.2, 18.63) * mm, "mid": v(120.3, 19.05) * mm, "end": v(120.45, 19.45) * mm});
            skArc(sketch, "E337", {"start": v(120.45, 19.45) * mm, "mid": v(122.2, 23.97) * mm, "end": v(123.69, 28.57) * mm});
            skArc(sketch, "E338", {"start": v(123.69, 28.57) * mm, "mid": v(124.87, 33.12) * mm, "end": v(125.77, 37.73) * mm});
            skArc(sketch, "E339", {"start": v(125.77, 37.73) * mm, "mid": v(126.38, 42.35) * mm, "end": v(126.7, 47) * mm});
            skArc(sketch, "E340", {"start": v(126.7, 47) * mm, "mid": v(126.74, 51.72) * mm, "end": v(126.5, 56.44) * mm});
            skArc(sketch, "E341", {"start": v(126.5, 56.44) * mm, "mid": v(125.82, 62.1) * mm, "end": v(124.72, 67.7) * mm});
            skArc(sketch, "E342", {"start": v(124.72, 67.7) * mm, "mid": v(123.23, 72.99) * mm, "end": v(121.3, 78.14) * mm});
            skArc(sketch, "E343", {"start": v(121.3, 78.14) * mm, "mid": v(119.33, 82.28) * mm, "end": v(116.98, 86.23) * mm});
            skArc(sketch, "E344", {"start": v(116.98, 86.23) * mm, "mid": v(115, 88.35) * mm, "end": v(112.45, 89.7) * mm});
            skArc(sketch, "E345", {"start": v(112.45, 89.7) * mm, "mid": v(108.52, 90.78) * mm, "end": v(104.5, 91.46) * mm});
            skArc(sketch, "E346", {"start": v(104.5, 91.46) * mm, "mid": v(99.27, 91.95) * mm, "end": v(94.03, 92.2) * mm});
            skArc(sketch, "E347", {"start": v(94.03, 92.2) * mm, "mid": v(88.35, 92.19) * mm, "end": v(82.69, 91.92) * mm});
            skArc(sketch, "E348", {"start": v(82.69, 91.92) * mm, "mid": v(77.29, 91.4) * mm, "end": v(71.93, 90.6) * mm});
            skArc(sketch, "E349", {"start": v(71.93, 90.6) * mm, "mid": v(68.74, 89.93) * mm, "end": v(65.6, 89.07) * mm});
            skArc(sketch, "E350", {"start": v(65.6, 89.07) * mm, "mid": v(61.67, 87.8) * mm, "end": v(57.79, 86.42) * mm});
            skArc(sketch, "E351", {"start": v(57.79, 86.42) * mm, "mid": v(54.12, 85) * mm, "end": v(50.48, 83.51) * mm});
            skArc(sketch, "E352", {"start": v(50.48, 83.51) * mm, "mid": v(49.04, 82.7) * mm, "end": v(47.8, 81.6) * mm});
            skArc(sketch, "E353", {"start": v(47.8, 81.6) * mm, "mid": v(47.25, 81.08) * mm, "end": v(46.62, 80.69) * mm});
            skArc(sketch, "E354", {"start": v(46.62, 80.69) * mm, "mid": v(46.04, 80.5) * mm, "end": v(45.43, 80.52) * mm});
            skArc(sketch, "E355", {"start": v(45.43, 80.52) * mm, "mid": v(44.52, 80.75) * mm, "end": v(43.65, 81.1) * mm});
            skArc(sketch, "E356", {"start": v(43.65, 81.1) * mm, "mid": v(41.47, 82.16) * mm, "end": v(39.3, 83.24) * mm});
            skArc(sketch, "E357", {"start": v(39.3, 83.24) * mm, "mid": v(35.9, 84.87) * mm, "end": v(32.45, 86.39) * mm});
            skArc(sketch, "E358", {"start": v(32.45, 86.39) * mm, "mid": v(29.13, 87.7) * mm, "end": v(25.75, 88.86) * mm});
            skArc(sketch, "E359", {"start": v(25.75, 88.86) * mm, "mid": v(22.3, 89.89) * mm, "end": v(18.8, 90.77) * mm});
            skArc(sketch, "E360", {"start": v(18.8, 90.77) * mm, "mid": v(15.02, 91.59) * mm, "end": v(11.21, 92.27) * mm});
            skArc(sketch, "E361", {"start": v(11.21, 92.27) * mm, "mid": v(8, 92.76) * mm, "end": v(4.77, 93.2) * mm});
            skArc(sketch, "E362", {"start": v(4.77, 93.2) * mm, "mid": v(2.6, 93.41) * mm, "end": v(0.43, 93.5) * mm});
            skArc(sketch, "E363", {"start": v(0.43, 93.5) * mm, "mid": v(-1.61, 93.47) * mm, "end": v(-3.64, 93.31) * mm});
            skArc(sketch, "E364", {"start": v(-3.64, 93.31) * mm, "mid": v(-6.35, 92.97) * mm, "end": v(-9.05, 92.56) * mm});
            skArc(sketch, "E365", {"start": v(-15.1, -19.78) * mm, "mid": v(-12.9, -20.94) * mm, "end": v(-10.71, -22.16) * mm});
            skArc(sketch, "E366", {"start": v(-10.71, -22.16) * mm, "mid": v(-8.92, -23.25) * mm, "end": v(-7.19, -24.42) * mm});
            skArc(sketch, "E367", {"start": v(-7.19, -24.42) * mm, "mid": v(-5.88, -25.38) * mm, "end": v(-4.62, -26.4) * mm});
            skArc(sketch, "E368", {"start": v(-4.62, -26.4) * mm, "mid": v(-4.22, -26.94) * mm, "end": v(-4.07, -27.6) * mm});
            skArc(sketch, "E369", {"start": v(-4.07, -27.6) * mm, "mid": v(-4.1, -27.75) * mm, "end": v(-4.22, -27.88) * mm});
            skArc(sketch, "E370", {"start": v(-4.22, -27.88) * mm, "mid": v(-4.4, -27.98) * mm, "end": v(-4.59, -28.03) * mm});
            skArc(sketch, "E371", {"start": v(-4.59, -28.03) * mm, "mid": v(-4.87, -28.04) * mm, "end": v(-5.15, -28) * mm});
            skArc(sketch, "E372", {"start": v(-5.15, -28) * mm, "mid": v(-5.5, -27.91) * mm, "end": v(-5.82, -27.8) * mm});
            skArc(sketch, "E373", {"start": v(-5.82, -27.8) * mm, "mid": v(-7.83, -27) * mm, "end": v(-9.85, -26.26) * mm});
            skArc(sketch, "E374", {"start": v(-9.85, -26.26) * mm, "mid": v(-12.9, -25.2) * mm, "end": v(-15.95, -24.15) * mm});
            skArc(sketch, "E375", {"start": v(-15.95, -24.15) * mm, "mid": v(-19.19, -23.07) * mm, "end": v(-22.44, -22.02) * mm});
            skArc(sketch, "E376", {"start": v(-22.44, -22.02) * mm, "mid": v(-25.21, -21.14) * mm, "end": v(-28, -20.3) * mm});
            skArc(sketch, "E377", {"start": v(-28, -20.3) * mm, "mid": v(-29.79, -19.77) * mm, "end": v(-31.56, -19.2) * mm});
            skArc(sketch, "E378", {"start": v(-31.56, -19.2) * mm, "mid": v(-32.53, -18.84) * mm, "end": v(-33.46, -18.4) * mm});
            skArc(sketch, "E379", {"start": v(-33.46, -18.4) * mm, "mid": v(-33.84, -18.12) * mm, "end": v(-34.13, -17.75) * mm});
            skArc(sketch, "E380", {"start": v(-34.13, -17.75) * mm, "mid": v(-34.18, -17.43) * mm, "end": v(-34, -17.16) * mm});
            skArc(sketch, "E381", {"start": v(-34, -17.16) * mm, "mid": v(-32.63, -16.5) * mm, "end": v(-31.13, -16.3) * mm});
            skArc(sketch, "E382", {"start": v(-31.13, -16.3) * mm, "mid": v(-28.43, -16.42) * mm, "end": v(-25.74, -16.7) * mm});
            skArc(sketch, "E383", {"start": v(-25.74, -16.7) * mm, "mid": v(-22.82, -17.21) * mm, "end": v(-19.93, -17.91) * mm});
            skArc(sketch, "E384", {"start": v(-19.93, -17.91) * mm, "mid": v(-17.47, -18.73) * mm, "end": v(-15.1, -19.78) * mm});
            skArc(sketch, "E385", {"start": v(-31.84, -21.79) * mm, "mid": v(-30.81, -22.25) * mm, "end": v(-29.82, -22.77) * mm});
            skArc(sketch, "E386", {"start": v(-29.82, -22.77) * mm, "mid": v(-29.01, -23.26) * mm, "end": v(-28.25, -23.82) * mm});
            skArc(sketch, "E387", {"start": v(-28.25, -23.82) * mm, "mid": v(-27.67, -24.33) * mm, "end": v(-27.15, -24.89) * mm});
            skArc(sketch, "E388", {"start": v(-27.15, -24.89) * mm, "mid": v(-26.83, -25.38) * mm, "end": v(-26.63, -25.93) * mm});
            skArc(sketch, "E389", {"start": v(-26.63, -25.93) * mm, "mid": v(-26.15, -27.17) * mm, "end": v(-25.4, -28.28) * mm});
            skArc(sketch, "E390", {"start": v(-25.4, -28.28) * mm, "mid": v(-24, -29.77) * mm, "end": v(-22.5, -31.17) * mm});
            skArc(sketch, "E391", {"start": v(-22.5, -31.17) * mm, "mid": v(-20.93, -32.45) * mm, "end": v(-19.27, -33.62) * mm});
            skArc(sketch, "E392", {"start": v(-19.27, -33.62) * mm, "mid": v(-18.18, -34.12) * mm, "end": v(-17, -34.3) * mm});
            skArc(sketch, "E393", {"start": v(-17, -34.3) * mm, "mid": v(-16.48, -34.26) * mm, "end": v(-15.96, -34.16) * mm});
            skArc(sketch, "E394", {"start": v(-15.96, -34.16) * mm, "mid": v(-15.18, -33.94) * mm, "end": v(-14.4, -33.7) * mm});
            skArc(sketch, "E395", {"start": v(-14.4, -33.7) * mm, "mid": v(-13.53, -33.38) * mm, "end": v(-12.67, -33.04) * mm});
            skArc(sketch, "E396", {"start": v(-12.67, -33.04) * mm, "mid": v(-11.82, -32.66) * mm, "end": v(-11, -32.25) * mm});
            skLineSegment(sketch, "E397", {"start": v(-11, -32.25) * mm, "end": v(-6.99, -30.21) * mm});
            skLineSegment(sketch, "E398", {"start": v(-6.99, -30.21) * mm, "end": v(-1.85, -33) * mm});
            skArc(sketch, "E399", {"start": v(-1.85, -33) * mm, "mid": v(0.82, -34.5) * mm, "end": v(3.45, -36.08) * mm});
            skArc(sketch, "E400", {"start": v(3.45, -36.08) * mm, "mid": v(3.9, -36.71) * mm, "end": v(3.75, -37.47) * mm});
            skArc(sketch, "E401", {"start": v(3.75, -37.47) * mm, "mid": v(3.04, -38.11) * mm, "end": v(2.11, -38.34) * mm});
            skArc(sketch, "E402", {"start": v(2.11, -38.34) * mm, "mid": v(-1.54, -38.25) * mm, "end": v(-5.2, -38.09) * mm});
            skArc(sketch, "E403", {"start": v(-5.2, -38.09) * mm, "mid": v(-9.35, -37.73) * mm, "end": v(-13.48, -37.1) * mm});
            skArc(sketch, "E404", {"start": v(-13.48, -37.1) * mm, "mid": v(-16.75, -36.28) * mm, "end": v(-19.9, -35.06) * mm});
            skArc(sketch, "E405", {"start": v(-19.9, -35.06) * mm, "mid": v(-22.91, -33.45) * mm, "end": v(-25.7, -31.48) * mm});
            skArc(sketch, "E406", {"start": v(-25.7, -31.48) * mm, "mid": v(-28.98, -28.7) * mm, "end": v(-32.07, -25.72) * mm});
            skArc(sketch, "E407", {"start": v(-32.07, -25.72) * mm, "mid": v(-33.29, -24.46) * mm, "end": v(-34.5, -23.19) * mm});
            skArc(sketch, "E408", {"start": v(-34.5, -23.19) * mm, "mid": v(-35.44, -22.16) * mm, "end": v(-36.36, -21.12) * mm});
            skArc(sketch, "E409", {"start": v(-36.36, -21.12) * mm, "mid": v(-37.01, -20.36) * mm, "end": v(-37.65, -19.59) * mm});
            skArc(sketch, "E410", {"start": v(-37.65, -19.59) * mm, "mid": v(-37.65, -19.46) * mm, "end": v(-37.54, -19.43) * mm});
            skArc(sketch, "E411", {"start": v(-37.54, -19.43) * mm, "mid": v(-37.22, -19.55) * mm, "end": v(-36.9, -19.67) * mm});
            skArc(sketch, "E412", {"start": v(-36.9, -19.67) * mm, "mid": v(-36.17, -19.97) * mm, "end": v(-35.44, -20.27) * mm});
            skArc(sketch, "E413", {"start": v(-35.44, -20.27) * mm, "mid": v(-34.57, -20.63) * mm, "end": v(-33.7, -21) * mm});
            skArc(sketch, "E414", {"start": v(-33.7, -21) * mm, "mid": v(-32.77, -21.4) * mm, "end": v(-31.84, -21.79) * mm});
            skArc(sketch, "E415", {"start": v(59.98, -31.82) * mm, "mid": v(61.17, -32.57) * mm, "end": v(62.21, -33.5) * mm});
            skArc(sketch, "E416", {"start": v(62.21, -33.5) * mm, "mid": v(62.38, -34.14) * mm, "end": v(61.93, -34.61) * mm});
            skArc(sketch, "E417", {"start": v(61.93, -34.61) * mm, "mid": v(60.24, -35.02) * mm, "end": v(58.52, -35.2) * mm});
            skArc(sketch, "E418", {"start": v(58.52, -35.2) * mm, "mid": v(53.89, -35.27) * mm, "end": v(49.26, -35.3) * mm});
            skArc(sketch, "E419", {"start": v(49.26, -35.3) * mm, "mid": v(46.66, -35.29) * mm, "end": v(44.06, -35.26) * mm});
            skArc(sketch, "E420", {"start": v(44.06, -35.26) * mm, "mid": v(41.9, -35.22) * mm, "end": v(39.76, -35.15) * mm});
            skArc(sketch, "E421", {"start": v(39.76, -35.15) * mm, "mid": v(37.97, -35.08) * mm, "end": v(36.18, -35) * mm});
            skArc(sketch, "E422", {"start": v(36.18, -35) * mm, "mid": v(36.07, -34.92) * mm, "end": v(36.1, -34.8) * mm});
            skArc(sketch, "E423", {"start": v(36.1, -34.8) * mm, "mid": v(36.73, -34.31) * mm, "end": v(37.46, -34.01) * mm});
            skArc(sketch, "E424", {"start": v(37.46, -34.01) * mm, "mid": v(40.92, -33.13) * mm, "end": v(44.4, -32.27) * mm});
            skArc(sketch, "E425", {"start": v(44.4, -32.27) * mm, "mid": v(47.71, -31.47) * mm, "end": v(51.05, -30.73) * mm});
            skArc(sketch, "E426", {"start": v(51.05, -30.73) * mm, "mid": v(52.63, -30.46) * mm, "end": v(54.23, -30.35) * mm});
            skArc(sketch, "E427", {"start": v(54.23, -30.35) * mm, "mid": v(54.87, -30.37) * mm, "end": v(55.51, -30.44) * mm});
            skArc(sketch, "E428", {"start": v(55.51, -30.44) * mm, "mid": v(56.3, -30.58) * mm, "end": v(57.07, -30.76) * mm});
            skArc(sketch, "E429", {"start": v(57.07, -30.76) * mm, "mid": v(57.86, -30.98) * mm, "end": v(58.64, -31.24) * mm});
            skArc(sketch, "E430", {"start": v(58.64, -31.24) * mm, "mid": v(59.32, -31.5) * mm, "end": v(59.98, -31.82) * mm});
            skArc(sketch, "E431", {"start": v(58.91, -38.55) * mm, "mid": v(58.4, -40.54) * mm, "end": v(57.06, -42.09) * mm});
            skArc(sketch, "E432", {"start": v(57.06, -42.09) * mm, "mid": v(54.46, -43.64) * mm, "end": v(51.65, -44.76) * mm});
            skArc(sketch, "E433", {"start": v(51.65, -44.76) * mm, "mid": v(48.03, -45.63) * mm, "end": v(44.33, -46.02) * mm});
            skArc(sketch, "E434", {"start": v(44.33, -46.02) * mm, "mid": v(40.57, -45.93) * mm, "end": v(36.84, -45.37) * mm});
            skArc(sketch, "E435", {"start": v(36.84, -45.37) * mm, "mid": v(34.78, -44.87) * mm, "end": v(32.75, -44.26) * mm});
            skArc(sketch, "E436", {"start": v(32.75, -44.26) * mm, "mid": v(31.08, -43.61) * mm, "end": v(29.47, -42.82) * mm});
            skArc(sketch, "E437", {"start": v(29.47, -42.82) * mm, "mid": v(28.47, -42.18) * mm, "end": v(27.56, -41.4) * mm});
            skArc(sketch, "E438", {"start": v(27.56, -41.4) * mm, "mid": v(27.33, -40.84) * mm, "end": v(27.57, -40.28) * mm});
            skArc(sketch, "E439", {"start": v(27.57, -40.28) * mm, "mid": v(27.83, -40.07) * mm, "end": v(28.13, -39.92) * mm});
            skArc(sketch, "E440", {"start": v(28.13, -39.92) * mm, "mid": v(28.7, -39.7) * mm, "end": v(29.28, -39.5) * mm});
            skArc(sketch, "E441", {"start": v(29.28, -39.5) * mm, "mid": v(29.98, -39.28) * mm, "end": v(30.69, -39.09) * mm});
            skArc(sketch, "E442", {"start": v(30.69, -39.09) * mm, "mid": v(31.44, -38.91) * mm, "end": v(32.2, -38.76) * mm});
            skArc(sketch, "E443", {"start": v(32.2, -38.76) * mm, "mid": v(33.2, -38.59) * mm, "end": v(34.22, -38.43) * mm});
            skArc(sketch, "E444", {"start": v(34.22, -38.43) * mm, "mid": v(34.68, -38.42) * mm, "end": v(35.13, -38.49) * mm});
            skArc(sketch, "E445", {"start": v(35.13, -38.49) * mm, "mid": v(35.35, -38.62) * mm, "end": v(35.46, -38.86) * mm});
            skArc(sketch, "E446", {"start": v(35.46, -38.86) * mm, "mid": v(35.46, -39.23) * mm, "end": v(35.37, -39.58) * mm});
            skArc(sketch, "E447", {"start": v(35.37, -39.58) * mm, "mid": v(35.27, -40.46) * mm, "end": v(35.6, -41.28) * mm});
            skArc(sketch, "E448", {"start": v(35.6, -41.28) * mm, "mid": v(36.42, -42.15) * mm, "end": v(37.4, -42.83) * mm});
            skArc(sketch, "E449", {"start": v(37.4, -42.83) * mm, "mid": v(38.88, -43.5) * mm, "end": v(40.44, -43.93) * mm});
            skArc(sketch, "E450", {"start": v(40.44, -43.93) * mm, "mid": v(42.26, -44.2) * mm, "end": v(44.1, -44.3) * mm});
            skArc(sketch, "E451", {"start": v(44.1, -44.3) * mm, "mid": v(45.47, -44.26) * mm, "end": v(46.84, -44.17) * mm});
            skArc(sketch, "E452", {"start": v(46.84, -44.17) * mm, "mid": v(47.69, -44.02) * mm, "end": v(48.49, -43.72) * mm});
            skArc(sketch, "E453", {"start": v(48.49, -43.72) * mm, "mid": v(49.2, -43.3) * mm, "end": v(49.83, -42.75) * mm});
            skArc(sketch, "E454", {"start": v(49.83, -42.75) * mm, "mid": v(50.7, -41.8) * mm, "end": v(51.5, -40.8) * mm});
            skArc(sketch, "E455", {"start": v(51.5, -40.8) * mm, "mid": v(52.51, -39.64) * mm, "end": v(53.68, -38.64) * mm});
            skArc(sketch, "E456", {"start": v(53.68, -38.64) * mm, "mid": v(54.89, -37.89) * mm, "end": v(56.21, -37.36) * mm});
            skArc(sketch, "E457", {"start": v(56.21, -37.36) * mm, "mid": v(57.16, -37.22) * mm, "end": v(58.1, -37.4) * mm});
            skArc(sketch, "E458", {"start": v(58.1, -37.4) * mm, "mid": v(58.7, -37.84) * mm, "end": v(58.91, -38.55) * mm});
            skArc(sketch, "E459", {"start": v(-82.07, 76.75) * mm, "mid": v(-86.1, 73.21) * mm, "end": v(-89.98, 69.53) * mm});
            skArc(sketch, "E460", {"start": v(-89.98, 69.53) * mm, "mid": v(-94.65, 64.84) * mm, "end": v(-99.22, 60.06) * mm});
            skArc(sketch, "E461", {"start": v(-99.22, 60.06) * mm, "mid": v(-103.68, 55.24) * mm, "end": v(-108.1, 50.4) * mm});
            skArc(sketch, "E462", {"start": v(-108.1, 50.4) * mm, "mid": v(-108.82, 49.23) * mm, "end": v(-109.07, 47.9) * mm});
            skArc(sketch, "E463", {"start": v(-109.07, 47.9) * mm, "mid": v(-109.15, 47.65) * mm, "end": v(-109.36, 47.5) * mm});
            skArc(sketch, "E464", {"start": v(-109.36, 47.5) * mm, "mid": v(-110.1, 47.28) * mm, "end": v(-110.84, 47.1) * mm});
            skArc(sketch, "E465", {"start": v(-110.84, 47.1) * mm, "mid": v(-111.8, 46.9) * mm, "end": v(-112.78, 46.74) * mm});
            skArc(sketch, "E466", {"start": v(-112.78, 46.74) * mm, "mid": v(-114.61, 46.29) * mm, "end": v(-116.47, 45.91) * mm});
            skArc(sketch, "E467", {"start": v(-116.47, 46.36) * mm, "mid": v(-118.85, 45.9) * mm, "end": v(-121.15, 45.15) * mm});
            skArc(sketch, "E468", {"start": v(-121.15, 45.15) * mm, "mid": v(-123.77, 43.86) * mm, "end": v(-126.1, 42.12) * mm});
            skArc(sketch, "E469", {"start": v(-126.1, 42.12) * mm, "mid": v(-128.08, 40) * mm, "end": v(-129.63, 37.56) * mm});
            skArc(sketch, "E470", {"start": v(-129.63, 37.56) * mm, "mid": v(-130.82, 34.74) * mm, "end": v(-131.56, 31.77) * mm});
            skArc(sketch, "E471", {"start": v(-131.56, 31.77) * mm, "mid": v(-131.68, 29.2) * mm, "end": v(-131.18, 26.69) * mm});
            skArc(sketch, "E472", {"start": v(-131.18, 26.69) * mm, "mid": v(-130.06, 24.1) * mm, "end": v(-128.48, 21.78) * mm});
            skArc(sketch, "E473", {"start": v(-128.48, 21.78) * mm, "mid": v(-126.41, 19.68) * mm, "end": v(-124.01, 17.97) * mm});
            skArc(sketch, "E474", {"start": v(-124.01, 17.97) * mm, "mid": v(-121.4, 16.74) * mm, "end": v(-118.6, 16.01) * mm});
            skArc(sketch, "E475", {"start": v(-118.6, 16.01) * mm, "mid": v(-116.33, 15.8) * mm, "end": v(-114.07, 15.88) * mm});
            skArc(sketch, "E476", {"start": v(-114.07, 15.88) * mm, "mid": v(-111.51, 16.25) * mm, "end": v(-109, 16.85) * mm});
            skArc(sketch, "E477", {"start": v(-109, 16.85) * mm, "mid": v(-106.69, 17.63) * mm, "end": v(-104.45, 18.62) * mm});
            skArc(sketch, "E478", {"start": v(-104.45, 18.62) * mm, "mid": v(-102.89, 19.62) * mm, "end": v(-101.55, 20.9) * mm});
            skArc(sketch, "E479", {"start": v(-101.55, 20.9) * mm, "mid": v(-99.9, 23.3) * mm, "end": v(-98.75, 25.95) * mm});
            skArc(sketch, "E480", {"start": v(-98.75, 25.95) * mm, "mid": v(-98.13, 28.77) * mm, "end": v(-98.06, 31.66) * mm});
            skArc(sketch, "E481", {"start": v(-98.06, 31.66) * mm, "mid": v(-98.55, 34.55) * mm, "end": v(-99.58, 37.28) * mm});
            skArc(sketch, "E482", {"start": v(-99.58, 37.28) * mm, "mid": v(-101.13, 39.83) * mm, "end": v(-103.1, 42.05) * mm});
            skArc(sketch, "E483", {"start": v(-103.1, 42.05) * mm, "mid": v(-103.9, 42.78) * mm, "end": v(-104.72, 43.48) * mm});
            skArc(sketch, "E484", {"start": v(-104.72, 43.48) * mm, "mid": v(-105.44, 44.05) * mm, "end": v(-106.19, 44.59) * mm});
            skArc(sketch, "E485", {"start": v(-107.36, 44) * mm, "mid": v(-106.94, 43.45) * mm, "end": v(-106.49, 42.94) * mm});
            skArc(sketch, "E486", {"start": v(-106.49, 42.94) * mm, "mid": v(-105.92, 42.35) * mm, "end": v(-105.33, 41.8) * mm});
            skArc(sketch, "E487", {"start": v(-105.33, 41.8) * mm, "mid": v(-103.69, 39.96) * mm, "end": v(-102.45, 37.83) * mm});
            skArc(sketch, "E488", {"start": v(-102.45, 37.83) * mm, "mid": v(-101.61, 35.42) * mm, "end": v(-101.23, 32.9) * mm});
            skArc(sketch, "E489", {"start": v(-101.23, 32.9) * mm, "mid": v(-101.3, 30.3) * mm, "end": v(-101.85, 27.77) * mm});
            skArc(sketch, "E490", {"start": v(-101.85, 27.77) * mm, "mid": v(-102.83, 25.4) * mm, "end": v(-104.23, 23.23) * mm});
            skArc(sketch, "E491", {"start": v(-104.23, 23.23) * mm, "mid": v(-106.52, 20.9) * mm, "end": v(-109.28, 19.16) * mm});
            skArc(sketch, "E492", {"start": v(-109.28, 19.16) * mm, "mid": v(-112.35, 18.08) * mm, "end": v(-115.6, 17.73) * mm});
            skArc(sketch, "E493", {"start": v(-115.6, 17.73) * mm, "mid": v(-118.84, 18.1) * mm, "end": v(-121.91, 19.21) * mm});
            skArc(sketch, "E494", {"start": v(-121.91, 19.21) * mm, "mid": v(-124.68, 20.98) * mm, "end": v(-126.98, 23.32) * mm});
            skArc(sketch, "E495", {"start": v(-126.98, 23.32) * mm, "mid": v(-127.85, 24.64) * mm, "end": v(-128.48, 26.09) * mm});
            skArc(sketch, "E496", {"start": v(-128.48, 26.09) * mm, "mid": v(-128.85, 27.64) * mm, "end": v(-128.97, 29.23) * mm});
            skArc(sketch, "E497", {"start": v(-128.97, 29.23) * mm, "mid": v(-128.82, 31.02) * mm, "end": v(-128.42, 32.77) * mm});
            skArc(sketch, "E498", {"start": v(-128.42, 32.77) * mm, "mid": v(-127.7, 34.78) * mm, "end": v(-126.82, 36.72) * mm});
            skArc(sketch, "E499", {"start": v(-126.82, 36.72) * mm, "mid": v(-125.8, 38.48) * mm, "end": v(-124.57, 40.1) * mm});
            skArc(sketch, "E500", {"start": v(-124.57, 40.1) * mm, "mid": v(-123.2, 41.5) * mm, "end": v(-121.67, 42.69) * mm});
            skArc(sketch, "E501", {"start": v(-121.67, 42.69) * mm, "mid": v(-120, 43.66) * mm, "end": v(-118.22, 44.39) * mm});
            skArc(sketch, "E502", {"start": v(-118.22, 44.39) * mm, "mid": v(-116.29, 44.9) * mm, "end": v(-114.32, 45.16) * mm});
            skArc(sketch, "E503", {"start": v(-114.32, 45.16) * mm, "mid": v(-112.36, 45.39) * mm, "end": v(-110.44, 45.8) * mm});
            skArc(sketch, "E504", {"start": v(-110.44, 45.8) * mm, "mid": v(-108.93, 46.33) * mm, "end": v(-107.52, 47.11) * mm});
            skArc(sketch, "E505", {"start": v(-107.52, 47.11) * mm, "mid": v(-105.9, 48.34) * mm, "end": v(-104.42, 49.72) * mm});
            skArc(sketch, "E506", {"start": v(-104.42, 49.72) * mm, "mid": v(-101.86, 52.44) * mm, "end": v(-99.36, 55.2) * mm});
            skArc(sketch, "E507", {"start": v(-99.36, 55.2) * mm, "mid": v(-97.83, 56.92) * mm, "end": v(-96.3, 58.62) * mm});
            skArc(sketch, "E508", {"start": v(-96.3, 58.62) * mm, "mid": v(-94.6, 60.45) * mm, "end": v(-92.9, 62.27) * mm});
            skArc(sketch, "E509", {"start": v(-92.9, 62.27) * mm, "mid": v(-91.32, 63.95) * mm, "end": v(-89.72, 65.62) * mm});
            skArc(sketch, "E510", {"start": v(-89.72, 65.62) * mm, "mid": v(-88.54, 66.83) * mm, "end": v(-87.33, 68.02) * mm});
            skLineSegment(sketch, "E511", {"start": v(-87.33, 68.02) * mm, "end": v(-82.38, 72.83) * mm});
            skLineSegment(sketch, "E512", {"start": v(-82.38, 72.83) * mm, "end": v(-77.63, 59.1) * mm});
            skLineSegment(sketch, "E513", {"start": v(-77.63, 59.1) * mm, "end": v(-72.87, 45.37) * mm});
            skLineSegment(sketch, "E514", {"start": v(-72.87, 45.37) * mm, "end": v(-76.45, 33.29) * mm});
            skArc(sketch, "E515", {"start": v(-76.45, 33.29) * mm, "mid": v(-78.07, 27.57) * mm, "end": v(-79.53, 21.82) * mm});
            skArc(sketch, "E516", {"start": v(-79.53, 21.82) * mm, "mid": v(-80.5, 17.25) * mm, "end": v(-81.21, 12.64) * mm});
            skArc(sketch, "E517", {"start": v(-81.21, 12.64) * mm, "mid": v(-81.68, 8.02) * mm, "end": v(-81.9, 3.39) * mm});
            skArc(sketch, "E518", {"start": v(-81.9, 3.39) * mm, "mid": v(-81.92, -2.46) * mm, "end": v(-81.8, -8.3) * mm});
            skArc(sketch, "E519", {"start": v(-81.8, -8.3) * mm, "mid": v(-81.42, -14.86) * mm, "end": v(-80.77, -21.4) * mm});
            skArc(sketch, "E520", {"start": v(-80.77, -21.4) * mm, "mid": v(-79.85, -27.68) * mm, "end": v(-78.64, -33.91) * mm});
            skArc(sketch, "E521", {"start": v(-78.64, -33.91) * mm, "mid": v(-76.94, -41.01) * mm, "end": v(-74.97, -48.04) * mm});
            skArc(sketch, "E522", {"start": v(-74.97, -48.04) * mm, "mid": v(-72.1, -57.26) * mm, "end": v(-69.07, -66.43) * mm});
            skArc(sketch, "E523", {"start": v(-69.07, -66.43) * mm, "mid": v(-67.7, -70.9) * mm, "end": v(-66.62, -75.45) * mm});
            skArc(sketch, "E524", {"start": v(-66.62, -75.45) * mm, "mid": v(-65.5, -81.33) * mm, "end": v(-64.56, -87.23) * mm});
            skArc(sketch, "E525", {"start": v(-64.56, -87.23) * mm, "mid": v(-63.77, -93.43) * mm, "end": v(-63.16, -99.65) * mm});
            skArc(sketch, "E526", {"start": v(-63.16, -99.65) * mm, "mid": v(-62.82, -105.22) * mm, "end": v(-62.7, -110.8) * mm});
            skArc(sketch, "E527", {"start": v(-62.7, -110.8) * mm, "mid": v(-62.72, -113.43) * mm, "end": v(-62.77, -116.07) * mm});
            skArc(sketch, "E528", {"start": v(-62.77, -116.07) * mm, "mid": v(-62.84, -118.6) * mm, "end": v(-62.94, -121.15) * mm});
            skArc(sketch, "E529", {"start": v(-62.94, -121.15) * mm, "mid": v(-63.05, -123.32) * mm, "end": v(-63.18, -125.48) * mm});
            skArc(sketch, "E530", {"start": v(-63.18, -125.48) * mm, "mid": v(-63.3, -126.64) * mm, "end": v(-63.48, -127.8) * mm});
            skArc(sketch, "E531", {"start": v(-63.48, -127.8) * mm, "mid": v(-63.65, -128.76) * mm, "end": v(-63.8, -129.73) * mm});
            skArc(sketch, "E532", {"start": v(-63.8, -129.73) * mm, "mid": v(-63.84, -130.2) * mm, "end": v(-63.8, -130.67) * mm});
            skArc(sketch, "E533", {"start": v(-63.8, -130.67) * mm, "mid": v(-63.72, -130.83) * mm, "end": v(-63.54, -130.89) * mm});
            skArc(sketch, "E534", {"start": v(-63.54, -130.89) * mm, "mid": v(-63.3, -130.83) * mm, "end": v(-63.1, -130.7) * mm});
            skArc(sketch, "E535", {"start": v(-63.1, -130.7) * mm, "mid": v(-61.8, -128.88) * mm, "end": v(-61.21, -126.72) * mm});
            skArc(sketch, "E536", {"start": v(-61.21, -126.72) * mm, "mid": v(-60.69, -120) * mm, "end": v(-60.3, -113.26) * mm});
            skArc(sketch, "E537", {"start": v(-60.3, -113.26) * mm, "mid": v(-60.1, -105.98) * mm, "end": v(-60.13, -98.69) * mm});
            skArc(sketch, "E538", {"start": v(-60.13, -98.69) * mm, "mid": v(-60.43, -92.23) * mm, "end": v(-61.04, -85.8) * mm});
            skArc(sketch, "E539", {"start": v(-61.04, -85.8) * mm, "mid": v(-61.35, -83.62) * mm, "end": v(-61.75, -81.46) * mm});
            skArc(sketch, "E540", {"start": v(-61.75, -81.46) * mm, "mid": v(-62.53, -77.86) * mm, "end": v(-63.34, -74.27) * mm});
            skArc(sketch, "E541", {"start": v(-63.34, -74.27) * mm, "mid": v(-64.33, -70.15) * mm, "end": v(-65.35, -66.04) * mm});
            skArc(sketch, "E542", {"start": v(-65.35, -66.04) * mm, "mid": v(-66.43, -61.91) * mm, "end": v(-67.55, -57.8) * mm});
            skArc(sketch, "E543", {"start": v(-67.55, -57.8) * mm, "mid": v(-70.34, -47.7) * mm, "end": v(-73.1, -37.6) * mm});
            skArc(sketch, "E544", {"start": v(-73.1, -37.6) * mm, "mid": v(-74.4, -32.64) * mm, "end": v(-75.6, -27.65) * mm});
            skArc(sketch, "E545", {"start": v(-75.6, -27.65) * mm, "mid": v(-76.36, -24.05) * mm, "end": v(-76.98, -20.41) * mm});
            skArc(sketch, "E546", {"start": v(-76.98, -20.41) * mm, "mid": v(-77.53, -16.46) * mm, "end": v(-77.96, -12.5) * mm});
            skArc(sketch, "E547", {"start": v(-77.96, -12.5) * mm, "mid": v(-78.32, -6.24) * mm, "end": v(-78.24, 0.01) * mm});
            skArc(sketch, "E548", {"start": v(-78.24, 0.01) * mm, "mid": v(-77.7, 8.2) * mm, "end": v(-76.9, 16.38) * mm});
            skArc(sketch, "E549", {"start": v(-76.9, 16.38) * mm, "mid": v(-75.91, 24.19) * mm, "end": v(-74.7, 31.97) * mm});
            skArc(sketch, "E550", {"start": v(-74.7, 31.97) * mm, "mid": v(-73.68, 35.94) * mm, "end": v(-72.03, 39.7) * mm});
            skArc(sketch, "E551", {"start": v(-72.03, 39.7) * mm, "mid": v(-71.78, 40) * mm, "end": v(-71.45, 40.17) * mm});
            skArc(sketch, "E552", {"start": v(-71.45, 40.17) * mm, "mid": v(-71.14, 40.15) * mm, "end": v(-70.9, 39.95) * mm});
            skArc(sketch, "E553", {"start": v(-70.9, 39.95) * mm, "mid": v(-70.52, 39.22) * mm, "end": v(-70.2, 38.46) * mm});
            skArc(sketch, "E554", {"start": v(-70.2, 38.46) * mm, "mid": v(-69.34, 36.1) * mm, "end": v(-68.49, 33.73) * mm});
            skArc(sketch, "E555", {"start": v(-68.49, 33.73) * mm, "mid": v(-68.34, 33.36) * mm, "end": v(-68.18, 33) * mm});
            skArc(sketch, "E556", {"start": v(-68.18, 33) * mm, "mid": v(-68.07, 32.87) * mm, "end": v(-67.9, 32.81) * mm});
            skArc(sketch, "E557", {"start": v(-67.9, 32.81) * mm, "mid": v(-67.74, 32.84) * mm, "end": v(-67.6, 32.94) * mm});
            skArc(sketch, "E558", {"start": v(-67.6, 32.94) * mm, "mid": v(-67.37, 33.25) * mm, "end": v(-67.15, 33.57) * mm});
            skArc(sketch, "E559", {"start": v(-67.15, 33.57) * mm, "mid": v(-66.49, 35.3) * mm, "end": v(-66.5, 37.16) * mm});
            skArc(sketch, "E560", {"start": v(-66.5, 37.16) * mm, "mid": v(-67.56, 42.26) * mm, "end": v(-68.76, 47.32) * mm});
            skArc(sketch, "E561", {"start": v(-68.76, 47.32) * mm, "mid": v(-70.26, 52.81) * mm, "end": v(-71.96, 58.24) * mm});
            skArc(sketch, "E562", {"start": v(-71.96, 58.24) * mm, "mid": v(-73.7, 63.02) * mm, "end": v(-75.72, 67.7) * mm});
            skLineSegment(sketch, "E563", {"start": v(-75.72, 67.7) * mm, "end": v(-79.17, 75.2) * mm});
            skLineSegment(sketch, "E564", {"start": v(-79.17, 75.2) * mm, "end": v(-74.87, 78.92) * mm});
            skArc(sketch, "E565", {"start": v(-74.87, 78.92) * mm, "mid": v(-74.03, 79.64) * mm, "end": v(-73.17, 80.35) * mm});
            skArc(sketch, "E566", {"start": v(-73.17, 80.35) * mm, "mid": v(-72.4, 80.96) * mm, "end": v(-71.61, 81.56) * mm});
            skArc(sketch, "E567", {"start": v(-71.61, 81.56) * mm, "mid": v(-70.95, 82.04) * mm, "end": v(-70.29, 82.52) * mm});
            skArc(sketch, "E568", {"start": v(-70.29, 82.52) * mm, "mid": v(-70.07, 82.63) * mm, "end": v(-69.82, 82.67) * mm});
            skArc(sketch, "E569", {"start": v(-69.82, 82.67) * mm, "mid": v(-69.67, 82.7) * mm, "end": v(-69.53, 82.8) * mm});
            skArc(sketch, "E570", {"start": v(-69.53, 82.8) * mm, "mid": v(-69.4, 82.96) * mm, "end": v(-69.3, 83.14) * mm});
            skArc(sketch, "E571", {"start": v(-69.3, 83.14) * mm, "mid": v(-69.2, 83.38) * mm, "end": v(-69.13, 83.63) * mm});
            skArc(sketch, "E572", {"start": v(-69.13, 83.63) * mm, "mid": v(-69.09, 83.91) * mm, "end": v(-69.07, 84.2) * mm});
            skArc(sketch, "E573", {"start": v(-69.07, 84.2) * mm, "mid": v(-69.3, 84.84) * mm, "end": v(-69.9, 85.18) * mm});
            skArc(sketch, "E574", {"start": v(-69.9, 85.18) * mm, "mid": v(-70.8, 85.17) * mm, "end": v(-71.64, 84.86) * mm});
            skArc(sketch, "E575", {"start": v(-71.64, 84.86) * mm, "mid": v(-73.47, 83.72) * mm, "end": v(-75.2, 82.43) * mm});
            skArc(sketch, "E576", {"start": v(-75.2, 82.43) * mm, "mid": v(-78.65, 79.6) * mm, "end": v(-82.07, 76.75) * mm});
            skArc(sketch, "E577", {"start": v(22.5, -62.22) * mm, "mid": v(21.98, -62.74) * mm, "end": v(21.42, -63.2) * mm});
            skArc(sketch, "E578", {"start": v(21.42, -63.2) * mm, "mid": v(20.51, -63.85) * mm, "end": v(19.59, -64.47) * mm});
            skArc(sketch, "E579", {"start": v(19.59, -64.47) * mm, "mid": v(18.52, -65.14) * mm, "end": v(17.43, -65.77) * mm});
            skArc(sketch, "E580", {"start": v(17.43, -65.77) * mm, "mid": v(16.34, -66.37) * mm, "end": v(15.24, -66.93) * mm});
            skArc(sketch, "E581", {"start": v(15.24, -66.93) * mm, "mid": v(13.16, -67.97) * mm, "end": v(11.1, -69.04) * mm});
            skArc(sketch, "E582", {"start": v(11.1, -69.04) * mm, "mid": v(10.68, -69.44) * mm, "end": v(10.51, -69.98) * mm});
            skArc(sketch, "E583", {"start": v(10.51, -69.98) * mm, "mid": v(10.69, -70.35) * mm, "end": v(11.08, -70.41) * mm});
            skArc(sketch, "E584", {"start": v(11.08, -70.41) * mm, "mid": v(13.13, -69.7) * mm, "end": v(15.16, -68.95) * mm});
            skArc(sketch, "E585", {"start": v(15.16, -68.95) * mm, "mid": v(16.98, -68.17) * mm, "end": v(18.73, -67.25) * mm});
            skArc(sketch, "E586", {"start": v(18.73, -67.25) * mm, "mid": v(20.42, -66.19) * mm, "end": v(22.02, -65) * mm});
            skArc(sketch, "E587", {"start": v(22.02, -65) * mm, "mid": v(23.27, -63.93) * mm, "end": v(24.43, -62.76) * mm});
            skArc(sketch, "E588", {"start": v(24.43, -62.76) * mm, "mid": v(24.8, -62.06) * mm, "end": v(24.75, -61.27) * mm});
            skArc(sketch, "E589", {"start": v(24.75, -61.27) * mm, "mid": v(24.64, -61.09) * mm, "end": v(24.45, -61) * mm});
            skArc(sketch, "E590", {"start": v(24.45, -61) * mm, "mid": v(24.2, -60.97) * mm, "end": v(23.96, -61.03) * mm});
            skArc(sketch, "E591", {"start": v(23.96, -61.03) * mm, "mid": v(23.6, -61.21) * mm, "end": v(23.28, -61.45) * mm});
            skArc(sketch, "E592", {"start": v(23.28, -61.45) * mm, "mid": v(22.88, -61.83) * mm, "end": v(22.5, -62.22) * mm});
            skArc(sketch, "E593", {"start": v(-31.6, -69.35) * mm, "mid": v(-31.91, -70.37) * mm, "end": v(-31.68, -71.4) * mm});
            skArc(sketch, "E594", {"start": v(-31.68, -71.4) * mm, "mid": v(-29.12, -76.23) * mm, "end": v(-26.51, -81.04) * mm});
            skArc(sketch, "E595", {"start": v(-26.51, -81.04) * mm, "mid": v(-23.95, -85.57) * mm, "end": v(-21.3, -90.05) * mm});
            skArc(sketch, "E596", {"start": v(-21.3, -90.05) * mm, "mid": v(-19.71, -92.32) * mm, "end": v(-17.86, -94.37) * mm});
            skArc(sketch, "E597", {"start": v(-17.86, -94.37) * mm, "mid": v(-16.88, -95.26) * mm, "end": v(-15.84, -96.07) * mm});
            skArc(sketch, "E598", {"start": v(-15.84, -96.07) * mm, "mid": v(-14.65, -96.88) * mm, "end": v(-13.42, -97.62) * mm});
            skArc(sketch, "E599", {"start": v(-13.42, -97.62) * mm, "mid": v(-12.05, -98.34) * mm, "end": v(-10.65, -98.98) * mm});
            skArc(sketch, "E600", {"start": v(-10.65, -98.98) * mm, "mid": v(-9.13, -99.6) * mm, "end": v(-7.59, -100.14) * mm});
            skArc(sketch, "E601", {"start": v(-7.59, -100.14) * mm, "mid": v(-3.38, -101.32) * mm, "end": v(0.9, -102.11) * mm});
            skArc(sketch, "E602", {"start": v(0.9, -102.11) * mm, "mid": v(4.25, -102.25) * mm, "end": v(7.56, -101.74) * mm});
            skArc(sketch, "E603", {"start": v(7.56, -101.74) * mm, "mid": v(10.4, -100.66) * mm, "end": v(12.92, -98.97) * mm});
            skArc(sketch, "E604", {"start": v(12.92, -98.97) * mm, "mid": v(15.42, -96.53) * mm, "end": v(17.51, -93.73) * mm});
            skArc(sketch, "E605", {"start": v(17.51, -93.73) * mm, "mid": v(18.99, -91.69) * mm, "end": v(20.68, -89.82) * mm});
            skArc(sketch, "E606", {"start": v(20.68, -89.82) * mm, "mid": v(23.05, -87.6) * mm, "end": v(25.54, -85.5) * mm});
            skArc(sketch, "E607", {"start": v(25.54, -85.5) * mm, "mid": v(28.1, -83.56) * mm, "end": v(30.74, -81.76) * mm});
            skArc(sketch, "E608", {"start": v(30.74, -81.76) * mm, "mid": v(32.78, -80.64) * mm, "end": v(34.95, -79.79) * mm});
            skArc(sketch, "E609", {"start": v(34.95, -79.79) * mm, "mid": v(35.34, -79.65) * mm, "end": v(35.7, -79.5) * mm});
            skArc(sketch, "E610", {"start": v(35.7, -79.5) * mm, "mid": v(36.04, -79.33) * mm, "end": v(36.35, -79.13) * mm});
            skArc(sketch, "E611", {"start": v(36.35, -79.13) * mm, "mid": v(36.58, -78.96) * mm, "end": v(36.8, -78.76) * mm});
            skArc(sketch, "E612", {"start": v(36.8, -78.76) * mm, "mid": v(36.9, -78.62) * mm, "end": v(36.93, -78.44) * mm});
            skArc(sketch, "E613", {"start": v(36.93, -78.44) * mm, "mid": v(36.8, -78.07) * mm, "end": v(36.45, -77.86) * mm});
            skArc(sketch, "E614", {"start": v(36.45, -77.86) * mm, "mid": v(35.34, -77.68) * mm, "end": v(34.23, -77.56) * mm});
            skArc(sketch, "E615", {"start": v(34.23, -77.56) * mm, "mid": v(31.93, -77.39) * mm, "end": v(29.61, -77.25) * mm});
            skArc(sketch, "E616", {"start": v(29.61, -77.25) * mm, "mid": v(20.77, -76.81) * mm, "end": v(11.93, -76.38) * mm});
            skArc(sketch, "E617", {"start": v(11.93, -76.38) * mm, "mid": v(4.54, -75.96) * mm, "end": v(-2.85, -75.44) * mm});
            skArc(sketch, "E618", {"start": v(-2.85, -75.44) * mm, "mid": v(-8.24, -74.91) * mm, "end": v(-13.62, -74.2) * mm});
            skArc(sketch, "E619", {"start": v(-13.62, -74.2) * mm, "mid": v(-17.64, -73.47) * mm, "end": v(-21.63, -72.56) * mm});
            skArc(sketch, "E620", {"start": v(-21.63, -72.56) * mm, "mid": v(-24.6, -71.62) * mm, "end": v(-27.44, -70.36) * mm});
            skArc(sketch, "E621", {"start": v(-27.44, -70.36) * mm, "mid": v(-28.15, -70.02) * mm, "end": v(-28.87, -69.71) * mm});
            skArc(sketch, "E622", {"start": v(-28.87, -69.71) * mm, "mid": v(-29.51, -69.48) * mm, "end": v(-30.17, -69.3) * mm});
            skArc(sketch, "E623", {"start": v(-30.17, -69.3) * mm, "mid": v(-30.67, -69.2) * mm, "end": v(-31.18, -69.14) * mm});
            skArc(sketch, "E624", {"start": v(-31.18, -69.14) * mm, "mid": v(-31.42, -69.18) * mm, "end": v(-31.6, -69.35) * mm});
            skArc(sketch, "E625", {"start": v(-19.3, -75.81) * mm, "mid": v(-16.32, -76.73) * mm, "end": v(-13.29, -77.44) * mm});
            skArc(sketch, "E626", {"start": v(-13.29, -77.44) * mm, "mid": v(-8.85, -78.26) * mm, "end": v(-4.4, -78.96) * mm});
            skArc(sketch, "E627", {"start": v(-4.4, -78.96) * mm, "mid": v(0.27, -79.59) * mm, "end": v(4.95, -80.1) * mm});
            skArc(sketch, "E628", {"start": v(4.95, -80.1) * mm, "mid": v(8.82, -80.38) * mm, "end": v(12.7, -80.5) * mm});
            skArc(sketch, "E629", {"start": v(12.7, -80.5) * mm, "mid": v(14.3, -80.52) * mm, "end": v(15.9, -80.57) * mm});
            skArc(sketch, "E630", {"start": v(15.9, -80.57) * mm, "mid": v(17.29, -80.64) * mm, "end": v(18.67, -80.74) * mm});
            skArc(sketch, "E631", {"start": v(18.67, -80.74) * mm, "mid": v(19.81, -80.85) * mm, "end": v(20.96, -80.97) * mm});
            skArc(sketch, "E632", {"start": v(20.96, -80.97) * mm, "mid": v(21.21, -81.06) * mm, "end": v(21.4, -81.24) * mm});
            skArc(sketch, "E633", {"start": v(21.4, -81.24) * mm, "mid": v(21.57, -82.02) * mm, "end": v(21.23, -82.73) * mm});
            skArc(sketch, "E634", {"start": v(21.23, -82.73) * mm, "mid": v(19.44, -84.52) * mm, "end": v(17.58, -86.24) * mm});
            skArc(sketch, "E635", {"start": v(17.58, -86.24) * mm, "mid": v(15.62, -87.9) * mm, "end": v(13.58, -89.46) * mm});
            skArc(sketch, "E636", {"start": v(13.58, -89.46) * mm, "mid": v(12.26, -90.21) * mm, "end": v(10.81, -90.67) * mm});
            skArc(sketch, "E637", {"start": v(10.81, -90.67) * mm, "mid": v(5.97, -91.3) * mm, "end": v(1.1, -91.27) * mm});
            skArc(sketch, "E638", {"start": v(1.1, -91.27) * mm, "mid": v(-3.8, -90.58) * mm, "end": v(-8.57, -89.25) * mm});
            skArc(sketch, "E639", {"start": v(-8.57, -89.25) * mm, "mid": v(-12.92, -87.39) * mm, "end": v(-16.98, -84.94) * mm});
            skArc(sketch, "E640", {"start": v(-16.98, -84.94) * mm, "mid": v(-20.29, -82.16) * mm, "end": v(-23.05, -78.83) * mm});
            skArc(sketch, "E641", {"start": v(-23.05, -78.83) * mm, "mid": v(-24.12, -77.22) * mm, "end": v(-25.14, -75.58) * mm});
            skArc(sketch, "E642", {"start": v(-25.14, -75.58) * mm, "mid": v(-25.24, -75.05) * mm, "end": v(-24.96, -74.59) * mm});
            skArc(sketch, "E643", {"start": v(-24.96, -74.59) * mm, "mid": v(-24.4, -74.32) * mm, "end": v(-23.76, -74.35) * mm});
            skArc(sketch, "E644", {"start": v(-23.76, -74.35) * mm, "mid": v(-21.53, -75.06) * mm, "end": v(-19.3, -75.81) * mm});
            skArc(sketch, "E645", {"start": v(40.93, -125.55) * mm, "mid": v(40.57, -125.8) * mm, "end": v(40.15, -125.9) * mm});
            skArc(sketch, "E646", {"start": v(40.15, -125.9) * mm, "mid": v(36.45, -126.25) * mm, "end": v(32.75, -126.57) * mm});
            skArc(sketch, "E647", {"start": v(32.75, -126.57) * mm, "mid": v(29.3, -126.86) * mm, "end": v(25.85, -127.11) * mm});
            skArc(sketch, "E648", {"start": v(25.85, -127.11) * mm, "mid": v(23.51, -127.23) * mm, "end": v(21.18, -127.28) * mm});
            skArc(sketch, "E649", {"start": v(21.18, -127.28) * mm, "mid": v(20.75, -127.31) * mm, "end": v(20.32, -127.39) * mm});
            skArc(sketch, "E650", {"start": v(20.32, -127.39) * mm, "mid": v(19.94, -127.51) * mm, "end": v(19.59, -127.7) * mm});
            skArc(sketch, "E651", {"start": v(19.59, -127.7) * mm, "mid": v(19.32, -127.9) * mm, "end": v(19.1, -128.14) * mm});
            skArc(sketch, "E652", {"start": v(19.1, -128.14) * mm, "mid": v(18.97, -128.39) * mm, "end": v(18.93, -128.66) * mm});
            skArc(sketch, "E653", {"start": v(18.93, -128.66) * mm, "mid": v(19.11, -129.16) * mm, "end": v(19.57, -129.4) * mm});
            skArc(sketch, "E654", {"start": v(19.57, -129.4) * mm, "mid": v(21.26, -129.62) * mm, "end": v(22.96, -129.76) * mm});
            skArc(sketch, "E655", {"start": v(22.96, -129.76) * mm, "mid": v(25.8, -129.9) * mm, "end": v(28.66, -129.95) * mm});
            skArc(sketch, "E656", {"start": v(28.66, -129.95) * mm, "mid": v(34.17, -129.97) * mm, "end": v(39.68, -129.97) * mm});
            skArc(sketch, "E657", {"start": v(39.68, -129.97) * mm, "mid": v(45.22, -129.97) * mm, "end": v(50.76, -130) * mm});
            skArc(sketch, "E658", {"start": v(50.76, -130) * mm, "mid": v(54.07, -130.08) * mm, "end": v(57.38, -130.24) * mm});
            skArc(sketch, "E659", {"start": v(57.38, -130.24) * mm, "mid": v(59.64, -130.43) * mm, "end": v(61.9, -130.73) * mm});
            skArc(sketch, "E660", {"start": v(61.9, -130.73) * mm, "mid": v(63.68, -131.08) * mm, "end": v(65.43, -131.59) * mm});
            skArc(sketch, "E661", {"start": v(65.43, -131.59) * mm, "mid": v(66.47, -131.92) * mm, "end": v(67.53, -132.23) * mm});
            skArc(sketch, "E662", {"start": v(67.53, -132.23) * mm, "mid": v(68.6, -132.52) * mm, "end": v(69.7, -132.78) * mm});
            skArc(sketch, "E663", {"start": v(69.7, -132.78) * mm, "mid": v(70.66, -132.99) * mm, "end": v(71.64, -133.17) * mm});
            skArc(sketch, "E664", {"start": v(71.64, -133.17) * mm, "mid": v(72.28, -133.25) * mm, "end": v(72.93, -133.28) * mm});
            skArc(sketch, "E665", {"start": v(72.93, -133.28) * mm, "mid": v(73.74, -133.28) * mm, "end": v(74.55, -133.26) * mm});
            skArc(sketch, "E666", {"start": v(74.55, -133.26) * mm, "mid": v(74.68, -133.19) * mm, "end": v(74.7, -133.04) * mm});
            skArc(sketch, "E667", {"start": v(74.7, -133.04) * mm, "mid": v(74.6, -132.85) * mm, "end": v(74.45, -132.7) * mm});
            skArc(sketch, "E668", {"start": v(74.45, -132.7) * mm, "mid": v(73.41, -132.06) * mm, "end": v(72.37, -131.42) * mm});
            skArc(sketch, "E669", {"start": v(72.37, -131.42) * mm, "mid": v(71.58, -130.98) * mm, "end": v(70.76, -130.6) * mm});
            skArc(sketch, "E670", {"start": v(70.76, -130.6) * mm, "mid": v(69.54, -130.1) * mm, "end": v(68.3, -129.63) * mm});
            skArc(sketch, "E671", {"start": v(68.3, -129.63) * mm, "mid": v(66.93, -129.14) * mm, "end": v(65.53, -128.7) * mm});
            skArc(sketch, "E672", {"start": v(65.53, -128.7) * mm, "mid": v(64.18, -128.3) * mm, "end": v(62.83, -127.93) * mm});
            skArc(sketch, "E673", {"start": v(62.83, -127.93) * mm, "mid": v(59.96, -127.28) * mm, "end": v(57.07, -126.77) * mm});
            skArc(sketch, "E674", {"start": v(57.07, -126.77) * mm, "mid": v(53.4, -126.24) * mm, "end": v(49.7, -125.8) * mm});
            skArc(sketch, "E675", {"start": v(49.7, -125.8) * mm, "mid": v(46.02, -125.41) * mm, "end": v(42.33, -125.06) * mm});
            skArc(sketch, "E676", {"start": v(42.33, -125.06) * mm, "mid": v(41.57, -125.16) * mm, "end": v(40.93, -125.55) * mm});
            skLineSegment(sketch, "E677", {"start": v(-76.07, -131.28) * mm, "end": v(-82.57, -133.1) * mm});
            skLineSegment(sketch, "E678", {"start": v(-82.57, -133.1) * mm, "end": v(-76.07, -133.19) * mm});
            skArc(sketch, "E679", {"start": v(-76.07, -133.19) * mm, "mid": v(-73.57, -133.18) * mm, "end": v(-71.08, -133.11) * mm});
            skArc(sketch, "E680", {"start": v(-71.08, -133.11) * mm, "mid": v(-69.37, -132.97) * mm, "end": v(-67.69, -132.68) * mm});
            skArc(sketch, "E681", {"start": v(-67.69, -132.68) * mm, "mid": v(-66.7, -132.4) * mm, "end": v(-65.76, -131.95) * mm});
            skArc(sketch, "E682", {"start": v(-65.76, -131.95) * mm, "mid": v(-65.37, -131.5) * mm, "end": v(-65.36, -130.92) * mm});
            skArc(sketch, "E683", {"start": v(-65.36, -130.92) * mm, "mid": v(-65.72, -130.33) * mm, "end": v(-66.31, -129.97) * mm});
            skArc(sketch, "E684", {"start": v(-66.31, -129.97) * mm, "mid": v(-67.28, -129.75) * mm, "end": v(-68.27, -129.7) * mm});
            skArc(sketch, "E685", {"start": v(-68.27, -129.7) * mm, "mid": v(-69.83, -129.83) * mm, "end": v(-71.38, -130.1) * mm});
            skArc(sketch, "E686", {"start": v(-71.38, -130.1) * mm, "mid": v(-73.73, -130.66) * mm, "end": v(-76.07, -131.28) * mm});
            skArc(sketch, "E687", {"start": v(15.62, -130.94) * mm, "mid": v(15.37, -131.33) * mm, "end": v(15.3, -131.8) * mm});
            skArc(sketch, "E688", {"start": v(15.3, -131.8) * mm, "mid": v(15.46, -132.25) * mm, "end": v(15.78, -132.58) * mm});
            skArc(sketch, "E689", {"start": v(15.78, -132.58) * mm, "mid": v(16.45, -132.92) * mm, "end": v(17.18, -133.11) * mm});
            skArc(sketch, "E690", {"start": v(17.18, -133.11) * mm, "mid": v(18.2, -133.23) * mm, "end": v(19.24, -133.26) * mm});
            skLineSegment(sketch, "E691", {"start": v(19.24, -133.26) * mm, "end": v(22.43, -133.22) * mm});
            skLineSegment(sketch, "E692", {"start": v(22.43, -133.22) * mm, "end": v(19.93, -131.8) * mm});
            skArc(sketch, "E693", {"start": v(19.93, -131.8) * mm, "mid": v(19, -131.27) * mm, "end": v(18.05, -130.77) * mm});
            skArc(sketch, "E694", {"start": v(18.05, -130.77) * mm, "mid": v(17.55, -130.56) * mm, "end": v(17.03, -130.42) * mm});
            skArc(sketch, "E695", {"start": v(17.03, -130.42) * mm, "mid": v(16.67, -130.4) * mm, "end": v(16.3, -130.48) * mm});
            skArc(sketch, "E696", {"start": v(16.3, -130.48) * mm, "mid": v(15.94, -130.67) * mm, "end": v(15.62, -130.94) * mm});
            skLineSegment(sketch, "E697", {"start": v(-37.72, 28.39) * mm, "end": v(-60.44, 31.27) * mm});
            skLineSegment(sketch, "E698", {"start": v(-67.9, 32.81) * mm, "end": v(-60.44, 31.27) * mm});
            skLineSegment(sketch, "E699", {"start": v(-116.58, 53.1) * mm, "end": v(-116.47, 45.91) * mm});
            skLineSegment(sketch, "E700", {"start": v(-63.1, -130.7) * mm, "end": v(8.38, -133.3) * mm});
            skLineSegment(sketch, "E701", {"start": v(81.2, -135.08) * mm, "end": v(53.09, -123.21) * mm});
            skLineSegment(sketch, "E702", {"start": v(53.09, -123.21) * mm, "end": v(9.23, -121.47) * mm});
            skLineSegment(sketch, "E703", {"start": v(81.2, -135.08) * mm, "end": v(9.11, -132.77) * mm});
            skCircle(sketch, "E704.converted", {"center": v(-115.79, 30.5) * mm, "radius": 17.04 * mm});
            skLineSegment(sketch, "E705", {"start": v(65.76, -50.26) * mm, "end": v(62.49, -42.88) * mm});
            skLineSegment(sketch, "E706", {"start": v(62.49, -42.88) * mm, "end": v(61.59, -39.87) * mm});
            skLineSegment(sketch, "E707", {"start": v(61.59, -39.87) * mm, "end": v(67.76, -33.3) * mm});
            skLineSegment(sketch, "E708", {"start": v(67.76, -33.3) * mm, "end": v(68.17, -22.21) * mm});
            skLineSegment(sketch, "E709", {"start": v(68.17, -22.21) * mm, "end": v(72.77, -13.2) * mm});
            skSolve(sketch);
        }
        {
            var Q0;
            Q0 = qSketchRegion(id + "F0", true);
            var Q1;
            Q1=makeQuery(id+"F0.imprint","IMPRINT",FACE,{"disambiguationData":[TD([[makeQuery(id+"F0.imprint","IMPRINT",EDGE,{"derivedFrom":sQuery(id+"F0.wireOp",EDGE,"E64")}),1.0]])]});
            extrude(context, id + "F1", {"entities" : qUnion([Q0, Q1]), "depth" : 30 * mm, "offsetDistance" : 25 * mm});
        }
        {
            var Q0;
            Q0 = qSketchRegion(id + "F0", true);
            extrude(context, id + "F2", {"entities" : qUnion([Q0]), "operationType" : NewBodyOperationType.ADD, "endBound" : BoundingType.SYMMETRIC, "depth" : 40 * mm, "offsetDistance" : 25 * mm, "hasSecondDirection" : true, "secondDirectionOppositeDirection" : true, "secondDirectionDepth" : 83 * mm});
        }
    });
